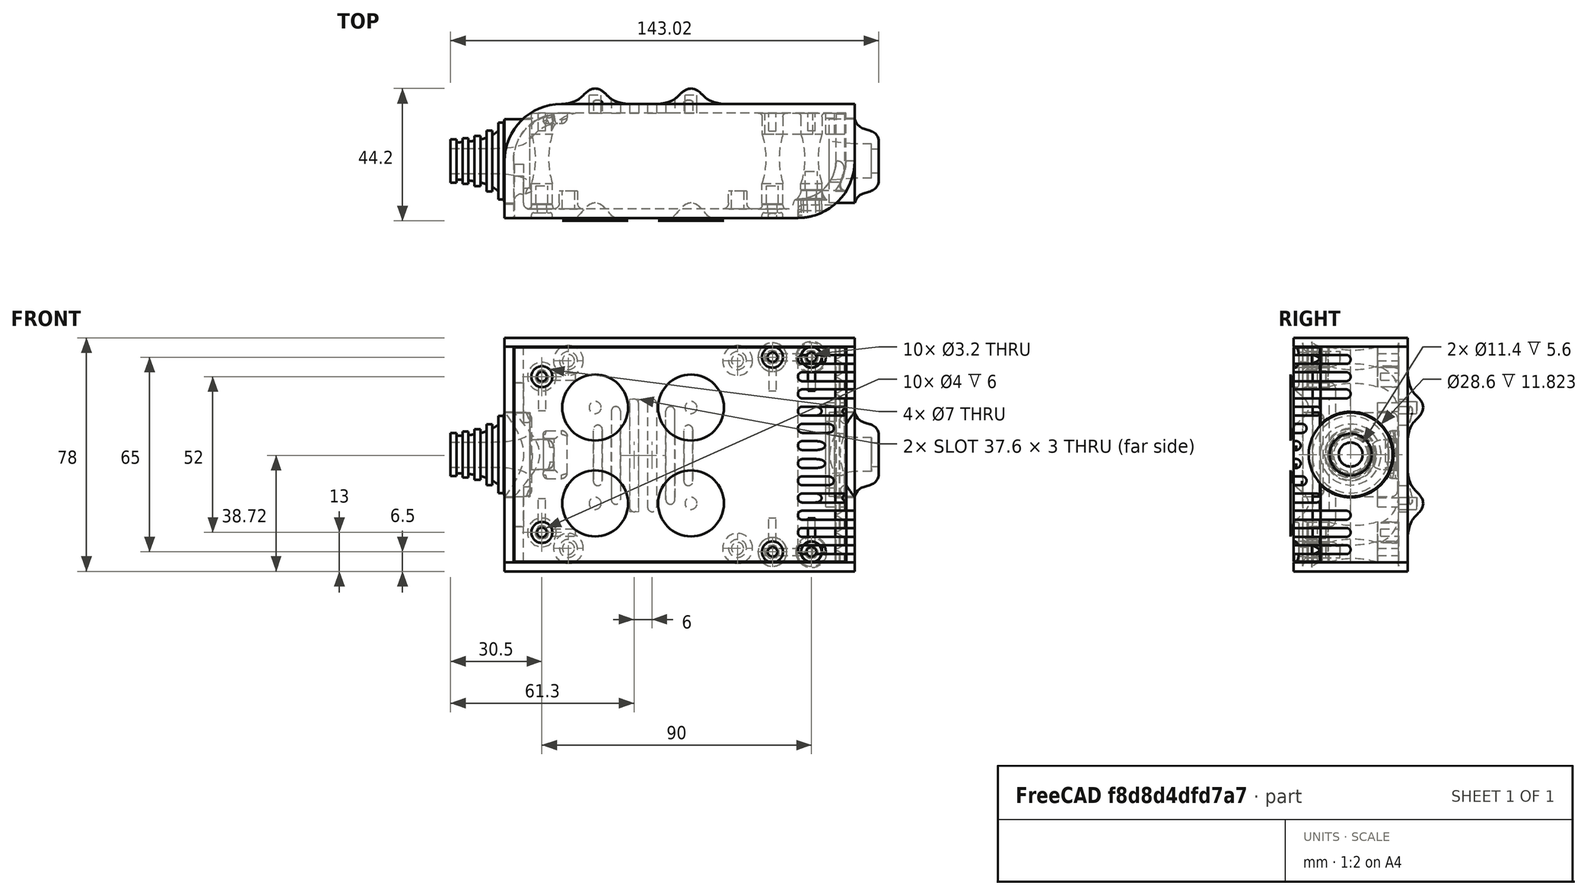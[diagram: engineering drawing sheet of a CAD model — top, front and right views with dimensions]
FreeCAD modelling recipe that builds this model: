
FCSTD DOCUMENT  (FreeCAD 0.19R0.19.2)
Label: enclosure_121
License: All rights reserved
LicenseURL: http://en.wikipedia.org/wiki/All_rights_reserved
objects: Part::Feature×72, Part::Revolution×72, Part::MultiFuse×54, Sketcher::SketchObject×34, Part::Fillet×26, Part::Cut×24, Part::Extrusion×23, Part::Cylinder×22, Part::Box×12, App::MeasureDistance×4
note: 339 computed .brp shape members not serialized (recipe doc carries the construction recipe); baked Part::Feature solids carry a one-line shape summary decoded from their .brp

FEATURE [Sketcher::SketchObject] Sketch  label="topSketch"
  FullyConstrained = true
  sketch-geometry (13):
    g0: LineSegment StartX=117 StartY=19 StartZ=0 EndX=117 EndY=38 EndZ=0
    g1: ArcOfCircle CenterX=98 CenterY=19 CenterZ=0 NormalX=0 NormalY=0 NormalZ=1 AngleXU=0 Radius=19 StartAngle=5.7297 EndAngle=6.28319
    g2: LineSegment StartX=0 StartY=3 StartZ=0 EndX=0 EndY=19 EndZ=0
    g3: LineSegment StartX=19 StartY=38 StartZ=0 EndX=117 EndY=38 EndZ=0
    g4: ArcOfCircle CenterX=19 CenterY=19 CenterZ=0 NormalX=0 NormalY=0 NormalZ=1 AngleXU=0 Radius=19 StartAngle=1.5708 EndAngle=3.14159
    g5: ArcOfCircle CenterX=19 CenterY=19 CenterZ=0 NormalX=0 NormalY=0 NormalZ=1 AngleXU=0 Radius=16 StartAngle=1.5708 EndAngle=3.14159
    g6: ArcOfCircle CenterX=98 CenterY=19 CenterZ=0 NormalX=0 NormalY=0 NormalZ=1 AngleXU=0 Radius=16 StartAngle=5.60905 EndAngle=6.28319
    g7: LineSegment StartX=114 StartY=19 StartZ=0 EndX=114 EndY=35 EndZ=0
    g8: LineSegment StartX=110.5 StartY=9.01251 StartZ=0 EndX=114.163 EndY=9.01251 EndZ=0
    g9: LineSegment StartX=114 StartY=35 StartZ=0 EndX=19 EndY=35 EndZ=0
    g10: LineSegment StartX=0 StartY=3 StartZ=0 EndX=0 EndY=0 EndZ=0
    g11: LineSegment StartX=3 StartY=0 StartZ=0 EndX=0 EndY=0 EndZ=0
    g12: LineSegment StartX=3 StartY=19 StartZ=0 EndX=3 EndY=0 EndZ=0
  constraints (33):
    c: Vertical(g0)
    c: Distance(g0) = 19
    c: Block(g0)
    c: Coincident(g1,g0)
    c: Block(g1)
    c: Vertical(g2)
    c: Block(g2)
    c: Coincident(g3,g0)
    c: Horizontal(g3)
    c: Distance(g3) = 98
    c: Coincident(g4,g3)
    c: Coincident(g4,g2)
    c: Block(g4)
    c: Coincident(g5,g4)
    c: Coincident(g6,g1)
    c: Block(g6)
    c: Block(g5)
    c: Coincident(g7,g6)
    c: Vertical(g7)
    c: Coincident(g8,g6)
    c: Coincident(g8,g1)
    c: Coincident(g9,g7)
    c: Coincident(g9,g5)
    c: Horizontal(g9)
    c: Tangent(g9,g5)
    c: Coincident(g10,g2)
    c: Distance(g10) = 3
    c: Vertical(g10)
    c: Coincident(g11,g10)
    c: Horizontal(g11)
    c: Coincident(g12,g5)
    c: Coincident(g12,g11)
    c: Vertical(g12)
FEATURE [Sketcher::SketchObject] Sketch001  label="bottomSketch"
  FullyConstrained = true
  sketch-geometry (32):
    g0: LineSegment StartX=3.3 StartY=-6.03275e-07 StartZ=0 EndX=98 EndY=-6.03275e-07 EndZ=0
    g1: ArcOfCircle CenterX=98 CenterY=19 CenterZ=0 NormalX=0 NormalY=0 NormalZ=1 AngleXU=0 Radius=19 StartAngle=4.71239 EndAngle=5.71103
    g2: LineSegment StartX=6.3 StartY=8 StartZ=0 EndX=3.3 EndY=8 EndZ=0
    g3: LineSegment StartX=3.3 StartY=8 StartZ=0 EndX=3.3 EndY=-6.03275e-07 EndZ=0
    g4: ArcOfCircle CenterX=8.3 CenterY=5 CenterZ=0 NormalX=0 NormalY=0 NormalZ=1 AngleXU=0 Radius=2 StartAngle=3.14159 EndAngle=4.71239
    g5: LineSegment StartX=6.3 StartY=8 StartZ=0 EndX=6.3 EndY=5 EndZ=0
    g6: ArcOfCircle CenterX=98 CenterY=19 CenterZ=0 NormalX=0 NormalY=0 NormalZ=1 AngleXU=0 Radius=12.7 StartAngle=4.71239 EndAngle=6.28319
    g7: LineSegment StartX=94.7 StartY=3 StartZ=0 EndX=8.3 EndY=3 EndZ=0
    g8-g12: Circle x5 (B-spline internal-alignment scaffolding for g13; pole/knot coordinates omitted)
    g13: BSplineCurve PolesCount=5 KnotsCount=3 Degree=3 IsPeriodic=0
    g14: GeomPoint X=98 Y=6.3 Z=0
    g15: GeomPoint X=96.3938 Y=4.71946 Z=0
    g16: GeomPoint X=94.7 Y=3 Z=0
    g17-g23: Circle x7 (B-spline internal-alignment scaffolding for g24; pole/knot coordinates omitted)
    g24: BSplineCurve PolesCount=7 KnotsCount=5 Degree=3 IsPeriodic=0
    g25-g29: GeomPoint x5 (B-spline internal-alignment scaffolding for g24; pole/knot coordinates omitted)
    g30: ArcOfCircle CenterX=98 CenterY=19 CenterZ=0 NormalX=0 NormalY=0 NormalZ=1 AngleXU=0 Radius=15.7 StartAngle=5.81226 EndAngle=6.28319
    g31: LineSegment StartX=110.7 StartY=19 StartZ=0 EndX=113.7 EndY=19 EndZ=0
  constraints (41):
    c: Horizontal(g0)
    c: Coincident(g1,g0)
    c: Block(g1)
    c: Horizontal(g2)
    c: Distance(g2) = 3
    c: Coincident(g3,g2)
    c: Vertical(g3)
    c: Coincident(g3,g0)
    c: Block(g4)
    c: Block(g2)
    c: Coincident(g5,g2)
    c: Coincident(g5,g4)
    c: Vertical(g5)
    c: Coincident(g6,g1)
    c: Block(g6)
    c: Coincident(g7,g4)
    c: Horizontal(g7)
    c: Block(g0)
    c: Block(g7)
    c: Block(g3)
    c: Coincident(g13,g6)
    c: Weight(g8) = 1
    c: Equal(g8, g9-g12) x4
    c: Coincident(g13,g7)
    c: InternalAlignment(g8-g12 -> g13) x5
    c: InternalAlignment(g14,g13)
    c: InternalAlignment(g15,g13)
    c: InternalAlignment(g16,g13)
    c: Block(g13)
    c: Weight(g17) = 1
    c: Equal(g17, g18-g23) x6
    c: Coincident(g24,g1)
    c: InternalAlignment(g17-g23 -> g24) x7
    c: InternalAlignment(g25-g29 -> g24) x5
    c: Block(g24)
    c: Coincident(g30,g24)
    c: Coincident(g31,g6)
    c: Coincident(g31,g30)
    c: Horizontal(g31)
    c: Block(g31)
    c: Block(g30)
FEATURE [Part::Extrusion] Extrude  label="top"
  Base = -> Sketch
  Dir = (0,0,1)
  DirMode = 2
  FaceMakerClass = Part::FaceMakerBullseye
  LengthFwd = 72
  LengthRev = 0
  Solid = true
  Symmetric = false
FEATURE [Part::Extrusion] Extrude001  label="bottom"
  Base = -> Sketch001
  Dir = (0,0,1)
  DirMode = 2
  FaceMakerClass = Part::FaceMakerBullseye
  LengthFwd = 71.4
  LengthRev = 0
  Placement = pos=(0,0,0.3) rot=(0,0,1;0rad)
  Solid = true
  Symmetric = false
FEATURE [Sketcher::SketchObject] Sketch002  label="topSketch001"
  FullyConstrained = true
  sketch-geometry (6):
    g0: LineSegment StartX=19 StartY=38 StartZ=0 EndX=117 EndY=38 EndZ=0
    g1: ArcOfCircle CenterX=19 CenterY=19 CenterZ=0 NormalX=0 NormalY=0 NormalZ=1 AngleXU=0 Radius=19 StartAngle=1.5708 EndAngle=3.14159
    g2: LineSegment StartX=117 StartY=38 StartZ=0 EndX=117 EndY=19 EndZ=0
    g3: LineSegment StartX=98 StartY=1.0161e-12 StartZ=0 EndX=5.22862e-06 EndY=1.0161e-12 EndZ=0
    g4: LineSegment StartX=5.22862e-06 StartY=19 StartZ=0 EndX=5.22862e-06 EndY=1.0161e-12 EndZ=0
    g5: ArcOfCircle CenterX=98 CenterY=19 CenterZ=0 NormalX=0 NormalY=0 NormalZ=1 AngleXU=0 Radius=19 StartAngle=4.71239 EndAngle=6.28319
  constraints (16):
    c: Horizontal(g0)
    c: Distance(g0) = 98
    c: Coincident(g1,g0)
    c: Block(g1)
    c: Coincident(g2,g0)
    c: Vertical(g2)
    c: Distance(g2) = 19
    c: Horizontal(g3)
    c: Coincident(g4,g1)
    c: Vertical(g4)
    c: Coincident(g3,g4)
    c: Block(g3)
    c: Coincident(g5,g2)
    c: Coincident(g5,g3)
    c: Block(g0)
    c: Block(g5)
FEATURE [Part::Extrusion] Extrude002  label="sideA"
  Base = -> Sketch002
  Dir = (0,0,1)
  DirMode = 2
  FaceMakerClass = Part::FaceMakerBullseye
  LengthFwd = 3
  LengthRev = 0
  Placement = pos=(0,0,-3) rot=(0,0,1;0rad)
  Solid = true
  Symmetric = false
FEATURE [Sketcher::SketchObject] Sketch003  label="topSketch002"
  FullyConstrained = true
  sketch-geometry (6):
    g0: LineSegment StartX=19 StartY=38 StartZ=0 EndX=117 EndY=38 EndZ=0
    g1: ArcOfCircle CenterX=19 CenterY=19 CenterZ=0 NormalX=0 NormalY=0 NormalZ=1 AngleXU=0 Radius=19 StartAngle=1.5708 EndAngle=3.14159
    g2: LineSegment StartX=117 StartY=38 StartZ=0 EndX=117 EndY=19 EndZ=0
    g3: LineSegment StartX=98 StartY=1.0161e-12 StartZ=0 EndX=5.22862e-06 EndY=1.0161e-12 EndZ=0
    g4: LineSegment StartX=5.22862e-06 StartY=19 StartZ=0 EndX=5.22862e-06 EndY=1.0161e-12 EndZ=0
    g5: ArcOfCircle CenterX=98 CenterY=19 CenterZ=0 NormalX=0 NormalY=0 NormalZ=1 AngleXU=0 Radius=19 StartAngle=4.71239 EndAngle=6.28319
  constraints (16):
    c: Horizontal(g0)
    c: Distance(g0) = 98
    c: Coincident(g1,g0)
    c: Block(g1)
    c: Coincident(g2,g0)
    c: Vertical(g2)
    c: Distance(g2) = 19
    c: Horizontal(g3)
    c: Coincident(g4,g1)
    c: Vertical(g4)
    c: Coincident(g3,g4)
    c: Block(g3)
    c: Coincident(g5,g2)
    c: Coincident(g5,g3)
    c: Block(g0)
    c: Block(g5)
FEATURE [Part::Extrusion] Extrude003  label="sideB"
  Base = -> Sketch003
  Dir = (0,0,1)
  DirMode = 2
  FaceMakerClass = Part::FaceMakerBullseye
  LengthFwd = 3
  LengthRev = 0
  Placement = pos=(0,0,72) rot=(0,0,1;0rad)
  Solid = true
  Symmetric = false
FEATURE [Sketcher::SketchObject] Sketch004
  FullyConstrained = true
  MapMode = 3
  Placement = pos=(0,0,0) rot=(1,0,0;1.5708rad)
  Support = -> [Extrude]
  sketch-geometry (8):
    g0: Circle CenterX=80.351 CenterY=-67.6202 CenterZ=0 NormalX=0 NormalY=0 NormalZ=1 AngleXU=0 Radius=2
    g1: Circle CenterX=80.351 CenterY=-67.6202 CenterZ=0 NormalX=0 NormalY=0 NormalZ=1 AngleXU=0 Radius=3
    g2: Circle CenterX=80.351 CenterY=-4.92017 CenterZ=0 NormalX=0 NormalY=0 NormalZ=1 AngleXU=0 Radius=2
    g3: Circle CenterX=80.351 CenterY=-4.92017 CenterZ=0 NormalX=0 NormalY=0 NormalZ=1 AngleXU=0 Radius=3
    g4: Circle CenterX=23.851 CenterY=-4.92017 CenterZ=0 NormalX=0 NormalY=0 NormalZ=1 AngleXU=0 Radius=2
    g5: Circle CenterX=23.851 CenterY=-4.92017 CenterZ=0 NormalX=0 NormalY=0 NormalZ=1 AngleXU=0 Radius=3
    g6: Circle CenterX=23.851 CenterY=-67.6202 CenterZ=0 NormalX=0 NormalY=0 NormalZ=1 AngleXU=0 Radius=2
    g7: Circle CenterX=23.851 CenterY=-67.6202 CenterZ=0 NormalX=0 NormalY=0 NormalZ=1 AngleXU=0 Radius=3
  constraints (8):
    c: Block(g3)
    c: Block(g2)
    c: Block(g1)
    c: Block(g0)
    c: Block(g6)
    c: Block(g7)
    c: Block(g4)
    c: Block(g5)
FEATURE [Part::Extrusion] Extrude004
  Base = -> Sketch004
  Dir = (0,-1,2e-16)
  DirMode = 2
  FaceMakerClass = Part::FaceMakerBullseye
  LengthFwd = 6
  LengthRev = 0
  Placement = pos=(0,9,0) rot=(0,0,1;0rad)
  Solid = true
  Symmetric = false
FEATURE [Sketcher::SketchObject] Sketch005
  FullyConstrained = true
  MapMode = 3
  Placement = pos=(0,0,0) rot=(1,0,0;1.5708rad)
  Support = -> [Extrude]
  sketch-geometry (8):
    g0: Circle CenterX=80.351 CenterY=-67.6202 CenterZ=0 NormalX=0 NormalY=0 NormalZ=1 AngleXU=0 Radius=3
    g1: Circle CenterX=80.351 CenterY=-4.92017 CenterZ=0 NormalX=0 NormalY=0 NormalZ=1 AngleXU=0 Radius=3
    g2: Circle CenterX=23.851 CenterY=-4.92017 CenterZ=0 NormalX=0 NormalY=0 NormalZ=1 AngleXU=0 Radius=3
    g3: Circle CenterX=23.851 CenterY=-67.6202 CenterZ=0 NormalX=0 NormalY=0 NormalZ=1 AngleXU=0 Radius=3
    g4: Circle CenterX=23.851 CenterY=-67.6202 CenterZ=0 NormalX=0 NormalY=0 NormalZ=1 AngleXU=0 Radius=5
    g5: Circle CenterX=80.351 CenterY=-67.6202 CenterZ=0 NormalX=0 NormalY=0 NormalZ=1 AngleXU=0 Radius=5
    g6: Circle CenterX=23.851 CenterY=-4.92017 CenterZ=0 NormalX=0 NormalY=0 NormalZ=1 AngleXU=0 Radius=5
    g7: Circle CenterX=80.351 CenterY=-4.92017 CenterZ=0 NormalX=0 NormalY=0 NormalZ=1 AngleXU=0 Radius=5
  constraints (8):
    c: Block(g1)
    c: Block(g0)
    c: Block(g3)
    c: Block(g2)
    c: Block(g5)
    c: Block(g4)
    c: Block(g6)
    c: Block(g7)
FEATURE [Part::Extrusion] Extrude005
  Base = -> Sketch005
  Dir = (0,-1,2e-16)
  DirMode = 2
  FaceMakerClass = Part::FaceMakerBullseye
  LengthFwd = 2
  LengthRev = 0
  Solid = true
  Symmetric = false
FEATURE [Sketcher::SketchObject] Sketch006
  FullyConstrained = true
  MapMode = 3
  Placement = pos=(0,0,0) rot=(1,0,0;1.5708rad)
  sketch-geometry (8):
    g0: Circle CenterX=80.351 CenterY=-67.6202 CenterZ=0 NormalX=0 NormalY=0 NormalZ=1 AngleXU=0 Radius=3
    g1: Circle CenterX=80.351 CenterY=-4.92017 CenterZ=0 NormalX=0 NormalY=0 NormalZ=1 AngleXU=0 Radius=3
    g2: Circle CenterX=23.851 CenterY=-4.92017 CenterZ=0 NormalX=0 NormalY=0 NormalZ=1 AngleXU=0 Radius=3
    g3: Circle CenterX=23.851 CenterY=-67.6202 CenterZ=0 NormalX=0 NormalY=0 NormalZ=1 AngleXU=0 Radius=3
    g4: Circle CenterX=23.851 CenterY=-67.6202 CenterZ=0 NormalX=0 NormalY=0 NormalZ=1 AngleXU=0 Radius=5
    g5: Circle CenterX=80.351 CenterY=-67.6202 CenterZ=0 NormalX=0 NormalY=0 NormalZ=1 AngleXU=0 Radius=5
    g6: Circle CenterX=23.851 CenterY=-4.92017 CenterZ=0 NormalX=0 NormalY=0 NormalZ=1 AngleXU=0 Radius=5
    g7: Circle CenterX=80.351 CenterY=-4.92017 CenterZ=0 NormalX=0 NormalY=0 NormalZ=1 AngleXU=0 Radius=5
  constraints (8):
    c: Block(g1)
    c: Block(g0)
    c: Block(g3)
    c: Block(g2)
    c: Block(g5)
    c: Block(g4)
    c: Block(g6)
    c: Block(g7)
FEATURE [Part::Extrusion] Extrude007
  Base = -> Sketch006
  Dir = (0,-1,2e-16)
  DirMode = 2
  FaceMakerClass = Part::FaceMakerBullseye
  LengthFwd = 2
  LengthRev = 0
  Solid = true
  Symmetric = false
FEATURE [Part::Fillet] Fillet
  Base = -> Extrude007
  Edges = 4 edges r=1.99: [Edge6,Edge12,Edge18,Edge24]
FEATURE [Part::Cut] Cut
  Base = -> Extrude005
  Placement = pos=(0,5,0) rot=(0,0,1;0rad)
  Tool = -> Fillet
FEATURE [Part::MultiFuse] Fusion  label="pCBScrews"
  Placement = pos=(-2.5,0,72.3) rot=(0,0,1;0rad)
  Shapes = -> [Extrude004,Cut]
FEATURE [App::MeasureDistance] Distance  label="Distance: 0.69 mm"
  Distance = 0.685967
  P1 = (24.0138,2.9647,0.3)
  P2 = (23.8901,3,-0.373787)
FEATURE [App::MeasureDistance] Distance001  label="Distance: 0.53 mm"
  Distance = 0.533607
  P1 = (80.2939,3,72.2334)
  P2 = (80.281,2.99661,71.7)
FEATURE [Part::Fillet] Fillet001
  Base = -> Extrude001
  Edges = 1 edges r=2.4: [Edge17]
FEATURE [Part::Fillet] Fillet002  label="bottom001"
  Base = -> Fillet001
  Edges = 1 edges r=2.4: [Edge36]
FEATURE [Part::Fillet] Fillet003  label="top001"
  Base = -> Extrude
  Edges = 1 edges r=2: [Edge1]
FEATURE [Sketcher::SketchObject] Sketch007
  FullyConstrained = true
  sketch-geometry (16):
    g0: LineSegment StartX=4 StartY=0 StartZ=0 EndX=4 EndY=2.4 EndZ=0
    g1: LineSegment StartX=4 StartY=2.4 StartZ=0 EndX=7 EndY=2.4 EndZ=0
    g2: LineSegment StartX=4 StartY=0 StartZ=0 EndX=5.7 EndY=0 EndZ=0
    g3: LineSegment StartX=5.7 StartY=0 StartZ=0 EndX=5.7 EndY=-5.6 EndZ=0
    g4-g8: Circle x5 (B-spline internal-alignment scaffolding for g9; pole/knot coordinates omitted)
    g9: BSplineCurve PolesCount=5 KnotsCount=3 Degree=3 IsPeriodic=0
    g10: GeomPoint X=7 Y=2.4 Z=0
    g11: GeomPoint X=10.4582 Y=-1.55472 Z=0
    g12: GeomPoint X=14 Y=-5.6 Z=0
    g13: LineSegment StartX=14 StartY=-5.6 StartZ=0 EndX=14 EndY=-14.1 EndZ=0
    g14: LineSegment StartX=14 StartY=-14.1 StartZ=0 EndX=6.5 EndY=-14.1 EndZ=0
    g15: LineSegment StartX=5.7 StartY=-5.6 StartZ=0 EndX=6.5 EndY=-14.1 EndZ=0
  constraints (28):
    c: Distance(g0) = 2.4
    c: Vertical(g0)
    c: Block(g0)
    c: Coincident(g1,g0)
    c: Horizontal(g1)
    c: Distance(g1) = 3
    c: Coincident(g2,g0)
    c: Horizontal(g2)
    c: Distance(g2) = 1.7
    c: Coincident(g3,g2)
    c: Vertical(g3)
    c: Distance(g3) = 5.6
    c: Coincident(g9,g1)
    c: Weight(g4) = 1
    c: Equal(g4, g5-g8) x4
    c: InternalAlignment(g4-g8 -> g9) x5
    c: InternalAlignment(g10,g9)
    c: InternalAlignment(g11,g9)
    c: InternalAlignment(g12,g9)
    c: Block(g9)
    c: Coincident(g13,g9)
    c: Vertical(g13)
    c: Distance(g13) = 8.5
    c: Coincident(g14,g13)
    c: Horizontal(g14)
    c: Distance(g14) = 7.5
    c: Coincident(g15,g3)
    c: Coincident(g15,g14)
FEATURE [Part::Feature] Face
  shape: bbox 10 x 16.5 x 2e-07 mm, 1 faces, 0 solids (baked)
FEATURE [Part::Revolution] Revolve  label="plugHousing"
  Angle = 360
  Axis = (0,1,0)
  Base = (0,0,0)
  FaceMakerClass = Part::FaceMakerBullseye
  Placement = pos=(0,0,36.15) rot=(0,0,1;0rad)
  Solid = false
  Source = -> Face
  Symmetric = false
FEATURE [Part::Feature] Face001
  shape: bbox 10 x 16.5 x 2e-07 mm, 1 faces, 0 solids (baked)
FEATURE [Part::Revolution] Revolve001  label="plugHousing001"
  Angle = 360
  Axis = (0,1,0)
  Base = (0,0,0)
  FaceMakerClass = Part::FaceMakerBullseye
  Placement = pos=(0,0,36.15) rot=(0,0,1;0rad)
  Solid = false
  Source = -> Face001
  Symmetric = false
FEATURE [Part::MultiFuse] Fusion001  label="plugHousing002"
  Placement = pos=(0,0,0) rot=(0,0,1;1.5708rad)
  Shapes = -> [Revolve001,Revolve]
FEATURE [Part::Feature] Face002
  shape: bbox 10 x 16.5 x 2e-07 mm, 1 faces, 0 solids (baked)
FEATURE [Part::Revolution] Revolve003  label="plugHousing005"
  Angle = 360
  Axis = (0,1,0)
  Base = (0,0,0)
  FaceMakerClass = Part::FaceMakerBullseye
  Placement = pos=(0,0,36.15) rot=(0,0,1;0rad)
  Solid = false
  Source = -> Face002
  Symmetric = false
FEATURE [Part::Feature] Face003
  shape: bbox 10 x 16.5 x 2e-07 mm, 1 faces, 0 solids (baked)
FEATURE [Part::Revolution] Revolve002  label="plugHousing003"
  Angle = 360
  Axis = (0,1,0)
  Base = (0,0,0)
  FaceMakerClass = Part::FaceMakerBullseye
  Placement = pos=(0,0,36.15) rot=(0,0,1;0rad)
  Solid = false
  Source = -> Face003
  Symmetric = false
FEATURE [Part::MultiFuse] Fusion002  label="plugHousing004"
  Placement = pos=(0,0,0) rot=(0,0,1;1.5708rad)
  Shapes = -> [Revolve002,Revolve003]
FEATURE [Part::MultiFuse] Fusion003  label="plugHousing006"
  Placement = pos=(0,19,0) rot=(0,0,1;3.14159rad)
  Shapes = -> [Fusion002,Fusion001]
FEATURE [Part::Feature] Face004
  shape: bbox 10 x 16.5 x 2e-07 mm, 1 faces, 0 solids (baked)
FEATURE [Part::Revolution] Revolve006  label="plugHousing010"
  Angle = 360
  Axis = (0,1,0)
  Base = (0,0,0)
  FaceMakerClass = Part::FaceMakerBullseye
  Placement = pos=(0,0,36.15) rot=(0,0,1;0rad)
  Solid = false
  Source = -> Face004
  Symmetric = false
FEATURE [Part::Feature] Face005
  shape: bbox 10 x 16.5 x 2e-07 mm, 1 faces, 0 solids (baked)
FEATURE [Part::Revolution] Revolve007  label="plugHousing011"
  Angle = 360
  Axis = (0,1,0)
  Base = (0,0,0)
  FaceMakerClass = Part::FaceMakerBullseye
  Placement = pos=(0,0,36.15) rot=(0,0,1;0rad)
  Solid = false
  Source = -> Face005
  Symmetric = false
FEATURE [Part::Feature] Face006
  shape: bbox 10 x 16.5 x 2e-07 mm, 1 faces, 0 solids (baked)
FEATURE [Part::Revolution] Revolve004  label="plugHousing007"
  Angle = 360
  Axis = (0,1,0)
  Base = (0,0,0)
  FaceMakerClass = Part::FaceMakerBullseye
  Placement = pos=(0,0,36.15) rot=(0,0,1;0rad)
  Solid = false
  Source = -> Face006
  Symmetric = false
FEATURE [Part::MultiFuse] Fusion004  label="plugHousing009"
  Placement = pos=(0,0,0) rot=(0,0,1;1.5708rad)
  Shapes = -> [Revolve004,Revolve007]
FEATURE [Part::Feature] Face007
  shape: bbox 10 x 16.5 x 2e-07 mm, 1 faces, 0 solids (baked)
FEATURE [Part::Revolution] Revolve005  label="plugHousing008"
  Angle = 360
  Axis = (0,1,0)
  Base = (0,0,0)
  FaceMakerClass = Part::FaceMakerBullseye
  Placement = pos=(0,0,36.15) rot=(0,0,1;0rad)
  Solid = false
  Source = -> Face007
  Symmetric = false
FEATURE [Part::MultiFuse] Fusion005  label="plugHousing012"
  Placement = pos=(0,0,0) rot=(0,0,1;1.5708rad)
  Shapes = -> [Revolve006,Revolve005]
FEATURE [Part::MultiFuse] Fusion006  label="plugHousing013"
  Placement = pos=(0,19,0) rot=(0,0,1;3.14159rad)
  Shapes = -> [Fusion005,Fusion004]
FEATURE [Part::MultiFuse] Fusion007  label="plugHousing014"
  Placement = pos=(122.621,0,-0.15) rot=(0,0,1;0rad)
  Shapes = -> [Fusion003,Fusion006]
FEATURE [Part::Cylinder] Cylinder002
  Angle = 360
  AttacherType = Attacher::AttachEngine3D
  Height = 20
  Placement = pos=(0,0,36.15) rot=(0,0,1;0rad)
  Radius = 4
FEATURE [Part::Cylinder] Cylinder003
  Angle = 360
  AttacherType = Attacher::AttachEngine3D
  Height = 10
  Placement = pos=(0,0,36.15) rot=(0,0,1;0rad)
  Radius = 4
FEATURE [Part::MultiFuse] Fusion009  label="removeToCreateHoleForPlugHousing"
  Placement = pos=(70,19,36.15) rot=(0,1,0;1.5708rad)
  Shapes = -> [Cylinder002,Cylinder003]
FEATURE [Part::Cylinder] Cylinder004
  Angle = 360
  AttacherType = Attacher::AttachEngine3D
  Height = 20
  Placement = pos=(0,0,36.15) rot=(0,0,1;0rad)
  Radius = 4
FEATURE [Part::Cylinder] Cylinder005
  Angle = 360
  AttacherType = Attacher::AttachEngine3D
  Height = 10
  Placement = pos=(0,0,36.15) rot=(0,0,1;0rad)
  Radius = 4
FEATURE [Part::MultiFuse] Fusion010  label="removeToCreateHoleForPlugHousing001"
  Placement = pos=(70,19,36.15) rot=(0,1,0;1.5708rad)
  Shapes = -> [Cylinder004,Cylinder005]
FEATURE [Part::Cut] Cut001
  Base = -> Fillet003
  Tool = -> Fusion010
FEATURE [Part::Cut] Cut002  label="Bottom"
  Base = -> Fillet002
  Tool = -> Fusion009
FEATURE [Part::Feature] Face008
  shape: bbox 10 x 16.5 x 2e-07 mm, 1 faces, 0 solids (baked)
FEATURE [Part::Revolution] Revolve011  label="plugHousing021"
  Angle = 360
  Axis = (0,1,0)
  Base = (0,0,0)
  FaceMakerClass = Part::FaceMakerBullseye
  Placement = pos=(0,0,36.15) rot=(0,0,1;0rad)
  Solid = false
  Source = -> Face008
  Symmetric = false
FEATURE [Part::Feature] Face009
  shape: bbox 10 x 16.5 x 2e-07 mm, 1 faces, 0 solids (baked)
FEATURE [Part::Revolution] Revolve012  label="plugHousing022"
  Angle = 360
  Axis = (0,1,0)
  Base = (0,0,0)
  FaceMakerClass = Part::FaceMakerBullseye
  Placement = pos=(0,0,36.15) rot=(0,0,1;0rad)
  Solid = false
  Source = -> Face009
  Symmetric = false
FEATURE [Part::Feature] Face010 .. Face013  x4 (patterned run collapsed; names and placements below)
  shape: bbox 10 x 16.5 x 2e-07 mm, 1 faces, 0 solids (baked)
FEATURE [Part::Revolution] Revolve015  label="plugHousing027"
  Angle = 360
  Axis = (0,1,0)
  Base = (0,0,0)
  FaceMakerClass = Part::FaceMakerBullseye
  Placement = pos=(0,0,36.15) rot=(0,0,1;0rad)
  Solid = false
  Source = -> Face013
  Symmetric = false
FEATURE [Part::Feature] Face014
  shape: bbox 10 x 16.5 x 2e-07 mm, 1 faces, 0 solids (baked)
FEATURE [Part::Feature] Face015
  shape: bbox 10 x 16.5 x 2e-07 mm, 1 faces, 0 solids (baked)
FEATURE [Part::Feature] Face016
  shape: bbox 10 x 16.5 x 2e-07 mm, 1 faces, 0 solids (baked)
FEATURE [Part::Revolution] Revolve019  label="plugHousing033"
  Angle = 360
  Axis = (0,1,0)
  Base = (0,0,0)
  FaceMakerClass = Part::FaceMakerBullseye
  Placement = pos=(0,0,36.15) rot=(0,0,1;0rad)
  Solid = false
  Source = -> Face016
  Symmetric = false
FEATURE [Part::Feature] Face017
  shape: bbox 10 x 16.5 x 2e-07 mm, 1 faces, 0 solids (baked)
FEATURE [Part::Revolution] Revolve020  label="plugHousing034"
  Angle = 360
  Axis = (0,1,0)
  Base = (0,0,0)
  FaceMakerClass = Part::FaceMakerBullseye
  Placement = pos=(0,0,36.15) rot=(0,0,1;0rad)
  Solid = false
  Source = -> Face017
  Symmetric = false
FEATURE [Part::Feature] Face018
  shape: bbox 10 x 16.5 x 2e-07 mm, 1 faces, 0 solids (baked)
FEATURE [Part::Revolution] Revolve016  label="plugHousing030"
  Angle = 360
  Axis = (0,1,0)
  Base = (0,0,0)
  FaceMakerClass = Part::FaceMakerBullseye
  Placement = pos=(0,0,36.15) rot=(0,0,1;0rad)
  Solid = false
  Source = -> Face018
  Symmetric = false
FEATURE [Part::MultiFuse] Fusion020  label="plugHousing038"
  Placement = pos=(0,0,0) rot=(0,0,1;1.5708rad)
  Shapes = -> [Revolve016,Revolve020]
FEATURE [Part::Feature] Face019
  shape: bbox 10 x 16.5 x 2e-07 mm, 1 faces, 0 solids (baked)
FEATURE [Part::Feature] Face020
  shape: bbox 10 x 16.5 x 2e-07 mm, 1 faces, 0 solids (baked)
FEATURE [Part::Revolution] Revolve017  label="plugHousing031"
  Angle = 360
  Axis = (0,1,0)
  Base = (0,0,0)
  FaceMakerClass = Part::FaceMakerBullseye
  Placement = pos=(0,0,36.15) rot=(0,0,1;0rad)
  Solid = false
  Source = -> Face020
  Symmetric = false
FEATURE [Part::MultiFuse] Fusion021  label="plugHousing039"
  Placement = pos=(0,0,0) rot=(0,0,1;1.5708rad)
  Shapes = -> [Revolve019,Revolve017]
FEATURE [Part::MultiFuse] Fusion023  label="plugHousing041"
  Placement = pos=(0,19,0) rot=(0,0,1;3.14159rad)
  Shapes = -> [Fusion021,Fusion020]
FEATURE [Part::Revolution] Revolve022  label="plugHousing043"
  Angle = 360
  Axis = (0,1,0)
  Base = (0,0,0)
  FaceMakerClass = Part::FaceMakerBullseye
  Placement = pos=(0,0,36.15) rot=(0,0,1;0rad)
  Solid = false
  Source = -> Face019
  Symmetric = false
FEATURE [Part::Feature] Face021
  shape: bbox 10 x 16.5 x 2e-07 mm, 1 faces, 0 solids (baked)
FEATURE [Part::Revolution] Revolve023  label="plugHousing044"
  Angle = 360
  Axis = (0,1,0)
  Base = (0,0,0)
  FaceMakerClass = Part::FaceMakerBullseye
  Placement = pos=(0,0,36.15) rot=(0,0,1;0rad)
  Solid = false
  Source = -> Face021
  Symmetric = false
FEATURE [Part::Feature] Face022
  shape: bbox 10 x 16.5 x 2e-07 mm, 1 faces, 0 solids (baked)
FEATURE [Part::Revolution] Revolve018  label="plugHousing032"
  Angle = 360
  Axis = (0,1,0)
  Base = (0,0,0)
  FaceMakerClass = Part::FaceMakerBullseye
  Placement = pos=(0,0,36.15) rot=(0,0,1;0rad)
  Solid = false
  Source = -> Face022
  Symmetric = false
FEATURE [Part::MultiFuse] Fusion022  label="plugHousing040"
  Placement = pos=(0,0,0) rot=(0,0,1;1.5708rad)
  Shapes = -> [Revolve018,Revolve023]
FEATURE [Part::Feature] Face023
  shape: bbox 10 x 16.5 x 2e-07 mm, 1 faces, 0 solids (baked)
FEATURE [Part::Revolution] Revolve021  label="plugHousing035"
  Angle = 360
  Axis = (0,1,0)
  Base = (0,0,0)
  FaceMakerClass = Part::FaceMakerBullseye
  Placement = pos=(0,0,36.15) rot=(0,0,1;0rad)
  Solid = false
  Source = -> Face023
  Symmetric = false
FEATURE [Part::MultiFuse] Fusion018  label="plugHousing036"
  Placement = pos=(0,0,0) rot=(0,0,1;1.5708rad)
  Shapes = -> [Revolve022,Revolve021]
FEATURE [Part::MultiFuse] Fusion019  label="plugHousing037"
  Placement = pos=(0,19,0) rot=(0,0,1;3.14159rad)
  Shapes = -> [Fusion018,Fusion022]
FEATURE [Part::MultiFuse] Fusion024  label="plugHousing042"
  Placement = pos=(122.621,0,-0.15) rot=(0,0,1;0rad)
  Shapes = -> [Fusion023,Fusion019]
FEATURE [Part::Cylinder] Cylinder006
  Angle = 360
  AttacherType = Attacher::AttachEngine3D
  Height = 20
  Placement = pos=(0,0,36.15) rot=(0,0,1;0rad)
  Radius = 14.3
FEATURE [Part::Cylinder] Cylinder007
  Angle = 360
  AttacherType = Attacher::AttachEngine3D
  Height = 10
  Placement = pos=(0,0,36.15) rot=(0,0,1;0rad)
  Radius = 4
FEATURE [Part::MultiFuse] Fusion026  label="removeToCreteHoleForPlugHousing"
  Placement = pos=(70,19,36) rot=(0,1,0;1.5708rad)
  Shapes = -> [Cylinder006,Cylinder007]
FEATURE [Part::Box] Box001  label="Cube001"
  AttacherType = Attacher::AttachEngine3D
  Height = 28
  Length = 3
  Placement = pos=(110.7,19,22) rot=(0,0,1;0rad)
  Width = 15.7
FEATURE [Part::Cut] Cut003  label="top002"
  Base = -> Cut001
  Tool = -> Fusion007
FEATURE [Part::Revolution] Revolve008  label="plugHousing015"
  Angle = 360
  Axis = (0,1,0)
  Base = (0,0,0)
  FaceMakerClass = Part::FaceMakerBullseye
  Placement = pos=(0,0,36.15) rot=(0,0,1;0rad)
  Solid = false
  Source = -> Face010
  Symmetric = false
FEATURE [Part::MultiFuse] Fusion013  label="plugHousing020"
  Placement = pos=(0,0,0) rot=(0,0,1;1.5708rad)
  Shapes = -> [Revolve008,Revolve012]
FEATURE [Part::Cut] Cut004  label="top003"
  Base = -> Cut003
  Placement = pos=(1,0,0) rot=(0,0,1;0rad)
  Tool = -> Fusion026
FEATURE [Part::Cylinder] Cylinder008
  Angle = 360
  AttacherType = Attacher::AttachEngine3D
  Height = 20
  Placement = pos=(0,0,36.15) rot=(0,0,1;0rad)
  Radius = 10.3
FEATURE [Part::Cylinder] Cylinder009
  Angle = 360
  AttacherType = Attacher::AttachEngine3D
  Height = 10
  Placement = pos=(0,0,36.15) rot=(0,0,1;0rad)
  Radius = 4
FEATURE [Part::MultiFuse] Fusion027  label="removeToCreteHoleForPlugHousing001"
  Placement = pos=(70,19,36) rot=(0,1,0;1.5708rad)
  Shapes = -> [Cylinder008,Cylinder009]
FEATURE [Part::Cut] Cut005  label="plugHousingTab"
  Base = -> Box001
  Tool = -> Fusion027
FEATURE [Part::MultiFuse] Fusion028  label="plugHousing045"
  Shapes = -> [Fusion024,Cut005]
FEATURE [Part::Box] Box002  label="Cube002"
  AttacherType = Attacher::AttachEngine3D
  Height = 28.8
  Length = 3
  Placement = pos=(107.3,28,21.6) rot=(0,0,1;0rad)
  Width = 7
FEATURE [Part::Box] Box003  label="Cube003"
  AttacherType = Attacher::AttachEngine3D
  Height = 3
  Length = 6.4
  Placement = pos=(107.3,28,18.6) rot=(0,0,1;0rad)
  Width = 7
FEATURE [Part::Box] Box004  label="Cube004"
  AttacherType = Attacher::AttachEngine3D
  Height = 3
  Length = 6.4
  Placement = pos=(107.3,28,50.4) rot=(0,0,1;0rad)
  Width = 7
FEATURE [Part::MultiFuse] Fusion029  label="plugHousingBracketHolder"
  Shapes = -> [Box004,Box002,Box003]
FEATURE [Part::Cylinder] Cylinder010
  Angle = 360
  AttacherType = Attacher::AttachEngine3D
  Height = 20
  Placement = pos=(0,0,36.15) rot=(0,0,1;0rad)
  Radius = 14.3
FEATURE [Part::Cylinder] Cylinder011
  Angle = 360
  AttacherType = Attacher::AttachEngine3D
  Height = 10
  Placement = pos=(0,0,36.15) rot=(0,0,1;0rad)
  Radius = 4
FEATURE [Part::MultiFuse] Fusion030  label="removeToCreteHoleForPlugHousing002"
  Placement = pos=(70,19,36) rot=(0,1,0;1.5708rad)
  Shapes = -> [Cylinder010,Cylinder011]
FEATURE [Part::Cut] Cut006  label="plugHousingBracketHolder001"
  Base = -> Fusion029
  Tool = -> Fusion030
FEATURE [Part::Cylinder] Cylinder012
  Angle = 360
  AttacherType = Attacher::AttachEngine3D
  Height = 20
  Placement = pos=(0,0,36.15) rot=(0,0,1;0rad)
  Radius = 7
FEATURE [Part::Cylinder] Cylinder013
  Angle = 360
  AttacherType = Attacher::AttachEngine3D
  Height = 10
  Placement = pos=(0,0,36.15) rot=(0,0,1;0rad)
  Radius = 4
FEATURE [Part::MultiFuse] Fusion032  label="removeToCreteHoleForPlugHousing003"
  Placement = pos=(70,19,36) rot=(0,1,0;1.5708rad)
  Shapes = -> [Cylinder012,Cylinder013]
FEATURE [Part::Cut] Cut007  label="bottom002"
  Base = -> Cut002
  Tool = -> Fusion032
FEATURE [Sketcher::SketchObject] Sketch008
  FullyConstrained = true
  sketch-geometry (54):
    g0: LineSegment StartX=-4.2 StartY=0 StartZ=0 EndX=-6.2 EndY=0 EndZ=0
    g1: LineSegment StartX=-14 StartY=-18 StartZ=0 EndX=-14 EndY=-26.5 EndZ=0
    g2: LineSegment StartX=-4.2 StartY=0 StartZ=0 EndX=-4.2 EndY=-13.4877 EndZ=0
    g3: Circle CenterX=-4.2 CenterY=-13.4877 CenterZ=0 NormalX=0 NormalY=0 NormalZ=1 AngleXU=0 Radius=1
    g4: Circle CenterX=-4.2 CenterY=-26.5 CenterZ=0 NormalX=0 NormalY=0 NormalZ=1 AngleXU=0 Radius=1
    g5: Circle CenterX=-8.2 CenterY=-26.5 CenterZ=0 NormalX=0 NormalY=0 NormalZ=1 AngleXU=0 Radius=1
    g6: BSplineCurve PolesCount=3 KnotsCount=2 Degree=2 IsPeriodic=0
    g7: GeomPoint X=-4.2 Y=-13.4877 Z=0
    g8: GeomPoint X=-8.2 Y=-26.5 Z=0
    g9: LineSegment StartX=-14 StartY=-26.5 StartZ=0 EndX=-8.2 EndY=-26.5 EndZ=0
    g10: LineSegment StartX=-10.15 StartY=-12 StartZ=0 EndX=-10.15 EndY=-14 EndZ=0
    g11: LineSegment StartX=-12.8401 StartY=-16 StartZ=0 EndX=-10.1571 EndY=-16 EndZ=0
    g12: LineSegment StartX=-10.15 StartY=-14 StartZ=0 EndX=-8.70761 EndY=-14 EndZ=0
    g13: LineSegment StartX=-12.8401 StartY=-16 StartZ=0 EndX=-12.8401 EndY=-17.6958 EndZ=0
    g14: LineSegment StartX=-10.15 StartY=-12 StartZ=0 EndX=-7.79258 EndY=-12 EndZ=0
    g15: Circle CenterX=-6.2215 CenterY=-2 CenterZ=0 NormalX=0 NormalY=0 NormalZ=1 AngleXU=0 Radius=1
    g16: Circle CenterX=-6.22762 CenterY=-2.58724 CenterZ=0 NormalX=0 NormalY=0 NormalZ=1 AngleXU=0 Radius=1
    g17: Circle CenterX=-6.32538 CenterY=-4 CenterZ=0 NormalX=0 NormalY=0 NormalZ=1 AngleXU=0 Radius=1
    g18: BSplineCurve PolesCount=3 KnotsCount=2 Degree=2 IsPeriodic=0
    g19: GeomPoint X=-6.2215 Y=-2 Z=0
    g20: GeomPoint X=-6.32538 Y=-4 Z=0
    g21: Circle CenterX=-6.48644 CenterY=-5.99526 CenterZ=0 NormalX=0 NormalY=0 NormalZ=1 AngleXU=0 Radius=1
    g22: Circle CenterX=-6.58486 CenterY=-6.99526 CenterZ=0 NormalX=0 NormalY=0 NormalZ=1 AngleXU=0 Radius=1
    g23: Circle CenterX=-6.77343 CenterY=-8 CenterZ=0 NormalX=0 NormalY=0 NormalZ=1 AngleXU=0 Radius=1
    g24: BSplineCurve PolesCount=3 KnotsCount=2 Degree=2 IsPeriodic=0
    g25: GeomPoint X=-6.48644 Y=-5.99526 Z=0
    g26: GeomPoint X=-6.77343 Y=-8 Z=0
    g27: Circle CenterX=-7.19003 CenterY=-10 CenterZ=0 NormalX=0 NormalY=0 NormalZ=1 AngleXU=0 Radius=1
    g28: Circle CenterX=-7.44407 CenterY=-11.0915 CenterZ=0 NormalX=0 NormalY=0 NormalZ=1 AngleXU=0 Radius=1
    g29: Circle CenterX=-7.79258 CenterY=-12 CenterZ=0 NormalX=0 NormalY=0 NormalZ=1 AngleXU=0 Radius=1
    g30: BSplineCurve PolesCount=3 KnotsCount=2 Degree=2 IsPeriodic=0
    g31: GeomPoint X=-7.19003 Y=-10 Z=0
    g32: GeomPoint X=-7.79258 Y=-12 Z=0
    g33: Circle CenterX=-8.70761 CenterY=-14 CenterZ=0 NormalX=0 NormalY=0 NormalZ=1 AngleXU=0 Radius=1
    g34: Circle CenterX=-9.33087 CenterY=-15.1837 CenterZ=0 NormalX=0 NormalY=0 NormalZ=1 AngleXU=0 Radius=1
    g35: Circle CenterX=-10.1571 CenterY=-16 CenterZ=0 NormalX=0 NormalY=0 NormalZ=1 AngleXU=0 Radius=1
    g36: BSplineCurve PolesCount=3 KnotsCount=2 Degree=2 IsPeriodic=0
    g37: GeomPoint X=-8.70761 Y=-14 Z=0
    g38: GeomPoint X=-10.1571 Y=-16 Z=0
    g39: Circle CenterX=-12.8401 CenterY=-17.6958 CenterZ=0 NormalX=0 NormalY=0 NormalZ=1 AngleXU=0 Radius=1
    g40: Circle CenterX=-13.3521 CenterY=-17.9027 CenterZ=0 NormalX=0 NormalY=0 NormalZ=1 AngleXU=0 Radius=1
    g41: Circle CenterX=-14 CenterY=-18 CenterZ=0 NormalX=0 NormalY=0 NormalZ=1 AngleXU=0 Radius=1
    g42: BSplineCurve PolesCount=3 KnotsCount=2 Degree=2 IsPeriodic=0
    g43: GeomPoint X=-12.8401 Y=-17.6958 Z=0
    g44: GeomPoint X=-14 Y=-18 Z=0
    g45: LineSegment StartX=-6.2 StartY=0 StartZ=0 EndX=-7.2 EndY=0 EndZ=0
    g46: LineSegment StartX=-7.2 StartY=0 StartZ=0 EndX=-7.2 EndY=-2 EndZ=0
    g47: LineSegment StartX=-7.2 StartY=-2 StartZ=0 EndX=-6.2215 EndY=-2 EndZ=0
    g48: LineSegment StartX=-6.32538 StartY=-4 StartZ=0 EndX=-7.65538 EndY=-4 EndZ=0
    g49: LineSegment StartX=-7.65538 StartY=-4 StartZ=0 EndX=-7.65538 EndY=-5.99526 EndZ=0
    g50: LineSegment StartX=-7.65538 StartY=-5.99526 StartZ=0 EndX=-6.48644 EndY=-5.99526 EndZ=0
    g51: LineSegment StartX=-6.77343 StartY=-8 StartZ=0 EndX=-8.43343 EndY=-8 EndZ=0
    g52: LineSegment StartX=-8.43343 StartY=-8 StartZ=0 EndX=-8.43343 EndY=-10 EndZ=0
    g53: LineSegment StartX=-8.43343 StartY=-10 StartZ=0 EndX=-7.19003 EndY=-10 EndZ=0
  constraints (112):
    c: Horizontal(g0)
    c: Distance(g0) = 2
    c: Block(g0)
    c: Vertical(g1)
    c: Coincident(g2,g0)
    c: Vertical(g2)
    c: Block(g2)
    c: Coincident(g6,g2)
    c: Weight(g3) = 1
    c: Equal(g3,g4)
    c: Equal(g3,g5)
    c: InternalAlignment(g3,g6)
    c: InternalAlignment(g4,g6)
    c: InternalAlignment(g5,g6)
    c: InternalAlignment(g7,g6)
    c: InternalAlignment(g8,g6)
    c: Block(g6)
    c: Coincident(g9,g1)
    c: Coincident(g9,g6)
    c: Horizontal(g9)
    c: Vertical(g10)
    c: Block(g10)
    c: Horizontal(g11)
    c: Block(g11)
    c: Coincident(g12,g10)
    c: Horizontal(g12)
    c: Block(g12)
    c: Coincident(g13,g11)
    c: Vertical(g13)
    c: Block(g13)
    c: Coincident(g14,g10)
    c: Horizontal(g14)
    c: Block(g14)
    c: Block(g9)
    c: Block(g1)
    c: Weight(g15) = 1
    c: Equal(g15,g16)
    c: Equal(g15,g17)
    c: InternalAlignment(g15,g18)
    c: InternalAlignment(g16,g18)
    c: InternalAlignment(g17,g18)
    c: InternalAlignment(g19,g18)
    c: InternalAlignment(g20,g18)
    c: Weight(g21) = 1
    c: Equal(g21,g22)
    c: Equal(g21,g23)
    c: InternalAlignment(g21,g24)
    c: InternalAlignment(g22,g24)
    c: InternalAlignment(g23,g24)
    c: InternalAlignment(g25,g24)
    c: InternalAlignment(g26,g24)
    c: Weight(g27) = 1
    c: Equal(g27,g28)
    c: Equal(g27,g29)
    c: Coincident(g30,g14)
    c: InternalAlignment(g27,g30)
    c: InternalAlignment(g28,g30)
    c: InternalAlignment(g29,g30)
    c: InternalAlignment(g31,g30)
    c: InternalAlignment(g32,g30)
    c: Coincident(g36,g12)
    c: Weight(g33) = 1
    c: Equal(g33,g34)
    c: Equal(g33,g35)
    c: Coincident(g36,g11)
    c: InternalAlignment(g33,g36)
    c: InternalAlignment(g34,g36)
    c: InternalAlignment(g35,g36)
    c: InternalAlignment(g37,g36)
    c: InternalAlignment(g38,g36)
    c: Coincident(g42,g13)
    c: Weight(g39) = 1
    c: Equal(g39,g40)
    c: Equal(g39,g41)
    c: Coincident(g42,g1)
    c: InternalAlignment(g39,g42)
    c: InternalAlignment(g40,g42)
    c: InternalAlignment(g41,g42)
    c: InternalAlignment(g43,g42)
    c: InternalAlignment(g44,g42)
    c: Block(g18)
    c: Block(g24)
    c: Block(g30)
    c: Block(g36)
    c: Block(g42)
    c: Horizontal(g45)
    c: Coincident(g45,g0)
    c: Vertical(g46)
    c: Coincident(g46,g45)
    c: Coincident(g47,g46)
    c: Coincident(g47,g18)
    c: Horizontal(g47)
    c: Block(g46)
    c: Coincident(g48,g18)
    c: Horizontal(g48)
    c: Distance(g48) = 1.33
    c: Vertical(g49)
    c: Coincident(g49,g48)
    c: Coincident(g50,g49)
    c: Coincident(g50,g24)
    c: Horizontal(g50)
    c: Tangent(g50,g22)
    c: Horizontal(g51)
    c: Coincident(g51,g24)
    c: Block(g51)
    c: Vertical(g52)
    c: Block(g52)
    c: Coincident(g52,g51)
    c: Coincident(g53,g52)
    c: Coincident(g53,g30)
    c: Horizontal(g53)
    c: Distance(g1) = 8.5
FEATURE [Part::Feature] Face024
  shape: bbox 9.8 x 26.5 x 2e-07 mm, 1 faces, 0 solids (baked)
FEATURE [Part::Revolution] Revolve024
  Angle = 360
  Axis = (0,1,0)
  Base = (0,0,0)
  FaceMakerClass = Part::FaceMakerBullseye
  Placement = pos=(0,0,0) rot=(0,0,1;1.5708rad)
  Solid = false
  Source = -> Face024
  Symmetric = false
FEATURE [Part::Feature] Face025
  shape: bbox 9.8 x 26.5 x 2e-07 mm, 1 faces, 0 solids (baked)
FEATURE [Part::Revolution] Revolve025
  Angle = 360
  Axis = (0,1,0)
  Base = (0,0,0)
  FaceMakerClass = Part::FaceMakerBullseye
  Placement = pos=(0,0,0) rot=(0,0,1;1.5708rad)
  Solid = false
  Source = -> Face025
  Symmetric = false
FEATURE [Part::MultiFuse] Fusion033
  Placement = pos=(-18,19,36) rot=(0,0,1;0rad)
  Shapes = -> [Revolve025,Revolve024]
FEATURE [Part::Cylinder] Cylinder014
  Angle = 360
  AttacherType = Attacher::AttachEngine3D
  Height = 20
  Placement = pos=(0,0,36.15) rot=(0,0,1;0rad)
  Radius = 14.3
FEATURE [Part::Cylinder] Cylinder015
  Angle = 360
  AttacherType = Attacher::AttachEngine3D
  Height = 10
  Placement = pos=(0,0,36.15) rot=(0,0,1;0rad)
  Radius = 4
FEATURE [Part::MultiFuse] Fusion034  label="removeToCreteHoleForPlugHousing004"
  Placement = pos=(-42,19,36) rot=(0,1,0;1.5708rad)
  Shapes = -> [Cylinder014,Cylinder015]
FEATURE [Part::Cut] Cut008  label="top004"
  Base = -> Cut004
  Placement = pos=(-1,0,0) rot=(0,0,1;0rad)
  Tool = -> Fusion034
FEATURE [Part::Box] Box005  label="Cube005"
  AttacherType = Attacher::AttachEngine3D
  Height = 28
  Length = 3
  Placement = pos=(110.7,19,22) rot=(0,0,1;0rad)
  Width = 15.7
FEATURE [Part::Cylinder] Cylinder016
  Angle = 360
  AttacherType = Attacher::AttachEngine3D
  Height = 10
  Placement = pos=(0,0,36.15) rot=(0,0,1;0rad)
  Radius = 4
FEATURE [Part::Cylinder] Cylinder017
  Angle = 360
  AttacherType = Attacher::AttachEngine3D
  Height = 20
  Placement = pos=(0,0,36.15) rot=(0,0,1;0rad)
  Radius = 10.3
FEATURE [Part::MultiFuse] Fusion035  label="removeToCreteHoleForPlugHousing005"
  Placement = pos=(70,19,36) rot=(0,1,0;1.5708rad)
  Shapes = -> [Cylinder017,Cylinder016]
FEATURE [Part::Cut] Cut009  label="plugHousingTab001"
  Base = -> Box005
  Placement = pos=(-107.4,-14,0) rot=(0,0,1;0rad)
  Tool = -> Fusion035
FEATURE [Part::Box] Box006  label="Cube006"
  AttacherType = Attacher::AttachEngine3D
  Height = 28
  Length = 3
  Placement = pos=(110.7,19,22) rot=(0,0,1;0rad)
  Width = 15.7
FEATURE [Part::Cylinder] Cylinder018
  Angle = 360
  AttacherType = Attacher::AttachEngine3D
  Height = 10
  Placement = pos=(0,0,36.15) rot=(0,0,1;0rad)
  Radius = 4
FEATURE [Part::Cylinder] Cylinder019
  Angle = 360
  AttacherType = Attacher::AttachEngine3D
  Height = 20
  Placement = pos=(0,0,36.15) rot=(0,0,1;0rad)
  Radius = 10.3
FEATURE [Part::MultiFuse] Fusion036  label="removeToCreteHoleForPlugHousing006"
  Placement = pos=(70,19,36) rot=(0,1,0;1.5708rad)
  Shapes = -> [Cylinder019,Cylinder018]
FEATURE [Part::Cut] Cut010  label="plugHousingTab002"
  Base = -> Box006
  Placement = pos=(-107.4,-14,0) rot=(0,0,1;0rad)
  Tool = -> Fusion036
FEATURE [Part::MultiFuse] Fusion037
  Placement = pos=(9.6,23,0) rot=(0,0,1;3.14159rad)
  Shapes = -> [Cut009,Cut010]
FEATURE [Part::Box] Box  label="Cube"
  AttacherType = Attacher::AttachEngine3D
  Height = 10
  Length = 3
  Placement = pos=(3.3,4,12) rot=(0,0,1;0rad)
  Width = 10
FEATURE [Part::Fillet] Fillet004
  Base = -> Fusion028
  Edges = 1 edges r=2: [Edge25]
FEATURE [Part::Fillet] Fillet005  label="plugHousing046"
  Base = -> Fillet004
  Edges = 1 edges r=2: [Edge8]
FEATURE [Part::Fillet] Fillet006
  Base = -> Box
  Edges = 1 edges r=2: [Edge11]
FEATURE [Part::Box] Box007  label="Cube007"
  AttacherType = Attacher::AttachEngine3D
  Height = 10
  Length = 3
  Placement = pos=(3.3,4,50) rot=(0,0,1;0rad)
  Width = 10
FEATURE [Part::Fillet] Fillet007
  Base = -> Box007
  Edges = 1 edges r=2: [Edge12]
FEATURE [Part::Box] Box008  label="Cube008"
  AttacherType = Attacher::AttachEngine3D
  Height = 28
  Length = 4
  Placement = pos=(5,0,22) rot=(0,0,1;0rad)
  Width = 10
FEATURE [Part::Fillet] Fillet008
  Base = -> Box008
  Edges = 1 edges r=1: [Edge7]
FEATURE [Part::Fillet] Fillet009
  Base = -> Fillet008
  Edges = 1 edges r=2: [Edge5]
FEATURE [Part::Fillet] Fillet010
  Base = -> Fillet009
  Edges = 1 edges r=2: [Edge2]
FEATURE [Sketcher::SketchObject] Sketch009  label="topSketch003"
  FullyConstrained = true
  sketch-geometry (4):
    g0: LineSegment StartX=16.8446 StartY=31.512 StartZ=0 EndX=16.3251 EndY=34.4666 EndZ=0
    g1: ArcOfCircle CenterX=19 CenterY=19.2524 CenterZ=0 NormalX=0 NormalY=0 NormalZ=1 AngleXU=0 Radius=15.4476 StartAngle=1.74483 EndAngle=2.72717
    g2: ArcOfCircle CenterX=19 CenterY=19.2524 CenterZ=0 NormalX=0 NormalY=0 NormalZ=1 AngleXU=0 Radius=12.4476 StartAngle=1.74483 EndAngle=2.73189
    g3: LineSegment StartX=4.86004 StartY=25.4725 StartZ=0 EndX=7.58253 EndY=24.2107 EndZ=0
  constraints (7):
    c: Block(g0)
    c: Coincident(g1,g0)
    c: Coincident(g2,g0)
    c: Coincident(g3,g1)
    c: Coincident(g3,g2)
    c: Block(g1)
    c: Block(g2)
FEATURE [Part::Extrusion] Extrude008
  Base = -> Sketch009
  Dir = (0,0,1)
  DirMode = 2
  FaceMakerClass = Part::FaceMakerBullseye
  LengthFwd = 10
  LengthRev = 0
  Placement = pos=(0,0,31) rot=(0,0,1;0rad)
  Solid = true
  Symmetric = false
FEATURE [Part::Cylinder] Cylinder020
  Angle = 360
  AttacherType = Attacher::AttachEngine3D
  Height = 20
  Placement = pos=(0,0,36.15) rot=(0,0,1;0rad)
  Radius = 8.2
FEATURE [Part::Cylinder] Cylinder021
  Angle = 360
  AttacherType = Attacher::AttachEngine3D
  Height = 10
  Placement = pos=(0,0,36.15) rot=(0,0,1;0rad)
  Radius = 4
FEATURE [Part::MultiFuse] Fusion038  label="removeToCreteHoleForPlugHousing007"
  Placement = pos=(-42,19,36) rot=(0,1,0;1.5708rad)
  Shapes = -> [Cylinder020,Cylinder021]
FEATURE [Part::Cut] Cut011
  Base = -> Extrude008
  Tool = -> Fusion038
FEATURE [Part::Fillet] Fillet011
  Base = -> Cut011
  Edges = 1 edges r=2: [Edge1]
FEATURE [Part::Fillet] Fillet012
  Base = -> Fillet011
  Edges = 1 edges r=2.5: [Edge1]
FEATURE [Part::Fillet] Fillet013
  Base = -> Fillet012
  Edges = 1 edges r=2.5: [Edge2]
FEATURE [Part::Box] Box010  label="Cube010"
  AttacherType = Attacher::AttachEngine3D
  Height = 16
  Length = 8
  Placement = pos=(12.7,31.52,28) rot=(0,0,1;0rad)
  Width = 4
FEATURE [Sketcher::SketchObject] Sketch010  label="topSketch004"
  FullyConstrained = true
  sketch-geometry (4):
    g0: LineSegment StartX=16.8446 StartY=31.512 StartZ=0 EndX=16.3251 EndY=34.4666 EndZ=0
    g1: ArcOfCircle CenterX=19 CenterY=19.2524 CenterZ=0 NormalX=0 NormalY=0 NormalZ=1 AngleXU=0 Radius=15.4476 StartAngle=1.74483 EndAngle=2.72717
    g2: ArcOfCircle CenterX=19 CenterY=19.2524 CenterZ=0 NormalX=0 NormalY=0 NormalZ=1 AngleXU=0 Radius=12.4476 StartAngle=1.74483 EndAngle=2.73189
    g3: LineSegment StartX=4.86004 StartY=25.4725 StartZ=0 EndX=7.58253 EndY=24.2107 EndZ=0
  constraints (7):
    c: Block(g0)
    c: Coincident(g1,g0)
    c: Coincident(g2,g0)
    c: Coincident(g3,g1)
    c: Coincident(g3,g2)
    c: Block(g1)
    c: Block(g2)
FEATURE [Part::Cylinder] Cylinder022
  Angle = 360
  AttacherType = Attacher::AttachEngine3D
  Height = 10
  Placement = pos=(0,0,36.15) rot=(0,0,1;0rad)
  Radius = 4
FEATURE [Sketcher::SketchObject] Sketch011  label="topSketch005"
  FullyConstrained = true
  sketch-geometry (4):
    g0: LineSegment StartX=16.8446 StartY=31.512 StartZ=0 EndX=16.3251 EndY=34.4666 EndZ=0
    g1: ArcOfCircle CenterX=19 CenterY=19.2524 CenterZ=0 NormalX=0 NormalY=0 NormalZ=1 AngleXU=0 Radius=15.4476 StartAngle=1.74483 EndAngle=2.72717
    g2: ArcOfCircle CenterX=19 CenterY=19.2524 CenterZ=0 NormalX=0 NormalY=0 NormalZ=1 AngleXU=0 Radius=12.4476 StartAngle=1.74483 EndAngle=2.73189
    g3: LineSegment StartX=4.86004 StartY=25.4725 StartZ=0 EndX=7.58253 EndY=24.2107 EndZ=0
  constraints (7):
    c: Block(g0)
    c: Coincident(g1,g0)
    c: Coincident(g2,g0)
    c: Coincident(g3,g1)
    c: Coincident(g3,g2)
    c: Block(g1)
    c: Block(g2)
FEATURE [Part::Extrusion] Extrude010
  Base = -> Sketch011
  Dir = (0,0,1)
  DirMode = 2
  FaceMakerClass = Part::FaceMakerBullseye
  LengthFwd = 10.6
  LengthRev = 0
  Placement = pos=(0,0,31) rot=(0,0,1;0rad)
  Solid = true
  Symmetric = false
FEATURE [Part::Cylinder] Cylinder023
  Angle = 360
  AttacherType = Attacher::AttachEngine3D
  Height = 20
  Placement = pos=(0,0,36.15) rot=(0,0,1;0rad)
  Radius = 8.2
FEATURE [Part::MultiFuse] Fusion039  label="removeToCreteHoleForPlugHousing008"
  Placement = pos=(-42,19,36) rot=(0,1,0;1.5708rad)
  Shapes = -> [Cylinder023,Cylinder022]
FEATURE [Part::Cut] Cut012
  Base = -> Extrude010
  Placement = pos=(0,0,-0.3) rot=(0,0,1;0rad)
  Tool = -> Fusion039
FEATURE [Part::Cut] Cut013
  Base = -> Box010
  Tool = -> Cut012
FEATURE [Part::Fillet] Fillet014
  Base = -> Cut013
  Edges = 1 edges r=0.7: [Edge13]
FEATURE [Part::Fillet] Fillet015
  Base = -> Fillet014
  Edges = 1 edges r=0.7: [Edge13]
FEATURE [Part::Fillet] Fillet016
  Base = -> Fillet015
  Edges = 1 edges r=0.7: [Edge16]
FEATURE [Part::Fillet] Fillet017
  Base = -> Fillet016
  Edges = 1 edges r=0.7: [Edge11]
FEATURE [Part::Fillet] Fillet018
  Base = -> Fillet017
  Edges = 1 edges r=0.7: [Edge10]
FEATURE [Part::Fillet] Fillet019
  Base = -> Fillet018
  Edges = 1 edges r=1.2: [Edge5]
FEATURE [Part::Fillet] Fillet020
  Base = -> Fillet019
  Edges = 1 edges r=1.2: [Edge12]
FEATURE [Part::Fillet] Fillet021
  Base = -> Fillet020
  Edges = 1 edges r=2: [Edge1]
  Placement = pos=(0.3,0,0) rot=(0,0,1;0rad)
FEATURE [Part::MultiFuse] Fusion040  label="top005"
  Shapes = -> [Cut008,Fillet021]
FEATURE [Part::MultiFuse] Fusion041  label="wireHolder"
  Shapes = -> [Fusion033,Fillet013]
FEATURE [Part::MultiFuse] Fusion042
  Shapes = -> [Fillet007,Fusion041]
FEATURE [Part::MultiFuse] Fusion043  label="wireHolder001"
  Shapes = -> [Fusion042,Fillet010]
FEATURE [Part::MultiFuse] Fusion044  label="wireHolder002"
  Shapes = -> [Fillet006,Fusion037,Fusion043]
FEATURE [Part::Feature] Face026
  shape: bbox 11 x 6 x 2e-07 mm, 1 faces, 0 solids (baked)
FEATURE [Part::Revolution] Revolve026
  Angle = 360
  Axis = (0,1,0)
  Base = (0,0,0)
  FaceMakerClass = Part::FaceMakerBullseye
  Placement = pos=(30.3,-1,19.7) rot=(0,0,1;0rad)
  Solid = false
  Source = -> Face026
  Symmetric = false
FEATURE [Sketcher::SketchObject] Sketch013  label="topSketch006"
  FullyConstrained = true
  sketch-geometry (13):
    g0: LineSegment StartX=117 StartY=19 StartZ=0 EndX=117 EndY=38 EndZ=0
    g1: ArcOfCircle CenterX=98 CenterY=19 CenterZ=0 NormalX=0 NormalY=0 NormalZ=1 AngleXU=0 Radius=19 StartAngle=5.7297 EndAngle=6.28319
    g2: LineSegment StartX=0 StartY=3 StartZ=0 EndX=0 EndY=19 EndZ=0
    g3: LineSegment StartX=19 StartY=38 StartZ=0 EndX=117 EndY=38 EndZ=0
    g4: ArcOfCircle CenterX=19 CenterY=19 CenterZ=0 NormalX=0 NormalY=0 NormalZ=1 AngleXU=0 Radius=19 StartAngle=1.5708 EndAngle=3.14159
    g5: ArcOfCircle CenterX=19 CenterY=19 CenterZ=0 NormalX=0 NormalY=0 NormalZ=1 AngleXU=0 Radius=16 StartAngle=1.5708 EndAngle=3.14159
    g6: ArcOfCircle CenterX=98 CenterY=19 CenterZ=0 NormalX=0 NormalY=0 NormalZ=1 AngleXU=0 Radius=16 StartAngle=5.60905 EndAngle=6.28319
    g7: LineSegment StartX=114 StartY=19 StartZ=0 EndX=114 EndY=35 EndZ=0
    g8: LineSegment StartX=110.5 StartY=9.01251 StartZ=0 EndX=114.163 EndY=9.01251 EndZ=0
    g9: LineSegment StartX=114 StartY=35 StartZ=0 EndX=19 EndY=35 EndZ=0
    g10: LineSegment StartX=0 StartY=3 StartZ=0 EndX=0 EndY=0 EndZ=0
    g11: LineSegment StartX=3 StartY=0 StartZ=0 EndX=0 EndY=0 EndZ=0
    g12: LineSegment StartX=3 StartY=19 StartZ=0 EndX=3 EndY=0 EndZ=0
  constraints (33):
    c: Vertical(g0)
    c: Distance(g0) = 19
    c: Block(g0)
    c: Coincident(g1,g0)
    c: Block(g1)
    c: Vertical(g2)
    c: Block(g2)
    c: Coincident(g3,g0)
    c: Horizontal(g3)
    c: Distance(g3) = 98
    c: Coincident(g4,g3)
    c: Coincident(g4,g2)
    c: Block(g4)
    c: Coincident(g5,g4)
    c: Coincident(g6,g1)
    c: Block(g6)
    c: Block(g5)
    c: Coincident(g7,g6)
    c: Vertical(g7)
    c: Coincident(g8,g6)
    c: Coincident(g8,g1)
    c: Coincident(g9,g7)
    c: Coincident(g9,g5)
    c: Horizontal(g9)
    c: Tangent(g9,g5)
    c: Coincident(g10,g2)
    c: Distance(g10) = 3
    c: Vertical(g10)
    c: Coincident(g11,g10)
    c: Horizontal(g11)
    c: Coincident(g12,g5)
    c: Coincident(g12,g11)
    c: Vertical(g12)
FEATURE [Part::Extrusion] Extrude011  label="top006"
  Base = -> Sketch013
  Dir = (0,0,1)
  DirMode = 2
  FaceMakerClass = Part::FaceMakerBullseye
  LengthFwd = 72
  LengthRev = 0
  Solid = true
  Symmetric = false
FEATURE [Sketcher::SketchObject] Sketch014
  FullyConstrained = true
  MapMode = 3
  Placement = pos=(0,0,0) rot=(1,0,0;1.5708rad)
  Support = -> [Extrude011]
  sketch-geometry (8):
    g0: Circle CenterX=80.351 CenterY=-67.6202 CenterZ=0 NormalX=0 NormalY=0 NormalZ=1 AngleXU=0 Radius=2
    g1: Circle CenterX=80.351 CenterY=-67.6202 CenterZ=0 NormalX=0 NormalY=0 NormalZ=1 AngleXU=0 Radius=3
    g2: Circle CenterX=80.351 CenterY=-4.92017 CenterZ=0 NormalX=0 NormalY=0 NormalZ=1 AngleXU=0 Radius=2
    g3: Circle CenterX=80.351 CenterY=-4.92017 CenterZ=0 NormalX=0 NormalY=0 NormalZ=1 AngleXU=0 Radius=3
    g4: Circle CenterX=23.851 CenterY=-4.92017 CenterZ=0 NormalX=0 NormalY=0 NormalZ=1 AngleXU=0 Radius=2
    g5: Circle CenterX=23.851 CenterY=-4.92017 CenterZ=0 NormalX=0 NormalY=0 NormalZ=1 AngleXU=0 Radius=3
    g6: Circle CenterX=23.851 CenterY=-67.6202 CenterZ=0 NormalX=0 NormalY=0 NormalZ=1 AngleXU=0 Radius=2
    g7: Circle CenterX=23.851 CenterY=-67.6202 CenterZ=0 NormalX=0 NormalY=0 NormalZ=1 AngleXU=0 Radius=3
  constraints (8):
    c: Block(g3)
    c: Block(g2)
    c: Block(g1)
    c: Block(g0)
    c: Block(g6)
    c: Block(g7)
    c: Block(g4)
    c: Block(g5)
FEATURE [Part::Feature] Face027
  shape: bbox 11 x 6 x 2e-07 mm, 1 faces, 0 solids (baked)
FEATURE [Part::Revolution] Revolve027
  Angle = 360
  Axis = (0,1,0)
  Base = (0,0,0)
  FaceMakerClass = Part::FaceMakerBullseye
  Placement = pos=(30.3,-1,51.7) rot=(0,0,1;0rad)
  Solid = false
  Source = -> Face027
  Symmetric = false
FEATURE [Part::Feature] Face028
  shape: bbox 11 x 6 x 2e-07 mm, 1 faces, 0 solids (baked)
FEATURE [Part::Revolution] Revolve028
  Angle = 360
  Axis = (0,1,0)
  Base = (0,0,0)
  FaceMakerClass = Part::FaceMakerBullseye
  Placement = pos=(62.3,-1,19.7) rot=(0,0,1;0rad)
  Solid = false
  Source = -> Face028
  Symmetric = false
FEATURE [Part::Feature] Face029
  shape: bbox 11 x 6 x 2e-07 mm, 1 faces, 0 solids (baked)
FEATURE [Part::Revolution] Revolve029
  Angle = 360
  Axis = (0,1,0)
  Base = (0,0,0)
  FaceMakerClass = Part::FaceMakerBullseye
  Placement = pos=(62.3,-1,51.7) rot=(0,0,1;0rad)
  Solid = false
  Source = -> Face029
  Symmetric = false
FEATURE [Part::Feature] Wire
  shape: bbox 11 x 5.2 x 2e-07 mm, 0 faces, 0 solids (baked)
FEATURE [Part::Revolution] Revolve030
  Angle = 360
  Axis = (0,1,0)
  Base = (0,0,0)
  FaceMakerClass = Part::FaceMakerBullseye
  Placement = pos=(30.3,38,19.7) rot=(0,0,1;0rad)
  Solid = true
  Source = -> Wire
  Symmetric = false
FEATURE [Part::Feature] Wire001
  shape: bbox 11 x 5.2 x 2e-07 mm, 0 faces, 0 solids (baked)
FEATURE [Part::Revolution] Revolve031
  Angle = 360
  Axis = (0,1,0)
  Base = (0,0,0)
  FaceMakerClass = Part::FaceMakerBullseye
  Placement = pos=(30.3,38,51.7) rot=(0,0,1;0rad)
  Solid = true
  Source = -> Wire001
  Symmetric = false
FEATURE [Part::Feature] Wire002
  shape: bbox 11 x 5.2 x 2e-07 mm, 0 faces, 0 solids (baked)
FEATURE [Part::Revolution] Revolve032
  Angle = 360
  Axis = (0,1,0)
  Base = (0,0,0)
  FaceMakerClass = Part::FaceMakerBullseye
  Placement = pos=(62.3,38,51.7) rot=(0,0,1;0rad)
  Solid = true
  Source = -> Wire002
  Symmetric = false
FEATURE [Part::Feature] Wire003
  shape: bbox 11 x 5.2 x 2e-07 mm, 0 faces, 0 solids (baked)
FEATURE [Part::Revolution] Revolve033
  Angle = 360
  Axis = (0,1,0)
  Base = (0,0,0)
  FaceMakerClass = Part::FaceMakerBullseye
  Placement = pos=(62.3,38,19.7) rot=(0,0,1;0rad)
  Solid = true
  Source = -> Wire003
  Symmetric = false
FEATURE [Part::MultiFuse] Fusion045  label="altRandScrewHousing"
  Shapes = -> [Revolve029,Revolve027,Revolve028,Revolve026]
FEATURE [Part::MultiFuse] Fusion046  label="fanScrewHousing"
  Shapes = -> [Revolve033,Revolve032,Revolve031,Revolve030]
FEATURE [Sketcher::SketchObject] Sketch015
  FullyConstrained = true
  sketch-geometry (17):
    g0: Circle CenterX=-3.5 CenterY=23.5 CenterZ=0 NormalX=0 NormalY=0 NormalZ=1 AngleXU=0 Radius=1
    g1: Circle CenterX=-1 CenterY=15.25 CenterZ=0 NormalX=0 NormalY=0 NormalZ=1 AngleXU=0 Radius=1
    g2: Circle CenterX=-3.5 CenterY=7 CenterZ=0 NormalX=0 NormalY=0 NormalZ=1 AngleXU=0 Radius=1
    g3: BSplineCurve PolesCount=3 KnotsCount=2 Degree=2 IsPeriodic=0
    g4: GeomPoint X=-3.5 Y=23.5 Z=0
    g5: GeomPoint X=-3.5 Y=7 Z=0
    g6: Circle CenterX=-4.8 CenterY=30.5 CenterZ=0 NormalX=0 NormalY=0 NormalZ=1 AngleXU=0 Radius=1
    g7: Circle CenterX=-3.5 CenterY=30.5 CenterZ=0 NormalX=0 NormalY=0 NormalZ=1 AngleXU=0 Radius=1
    g8: Circle CenterX=-3.5 CenterY=29.2 CenterZ=0 NormalX=0 NormalY=0 NormalZ=1 AngleXU=0 Radius=1
    g9: BSplineCurve PolesCount=3 KnotsCount=2 Degree=2 IsPeriodic=0
    g10: GeomPoint X=-4.8 Y=30.5 Z=0
    g11: GeomPoint X=-3.5 Y=29.2 Z=0
    g12: LineSegment StartX=-3.5 StartY=29.2 StartZ=0 EndX=-3.5 EndY=23.5 EndZ=0
    g13: LineSegment StartX=-4.8 StartY=30.5 StartZ=0 EndX=0 EndY=30.5 EndZ=0
    g14: LineSegment StartX=-3.5 StartY=0.3 StartZ=0 EndX=0 EndY=0.3 EndZ=0
    g15: LineSegment StartX=-3.5 StartY=0.3 StartZ=0 EndX=-3.5 EndY=7 EndZ=0
    g16: LineSegment StartX=0 StartY=0.3 StartZ=0 EndX=0 EndY=30.5 EndZ=0
  constraints (33):
    c: Weight(g0) = 1
    c: Equal(g0,g1)
    c: Equal(g0,g2)
    c: InternalAlignment(g0,g3)
    c: InternalAlignment(g1,g3)
    c: InternalAlignment(g2,g3)
    c: InternalAlignment(g4,g3)
    c: InternalAlignment(g5,g3)
    c: Block(g3)
    c: Weight(g6) = 1
    c: Equal(g6,g7)
    c: Equal(g6,g8)
    c: InternalAlignment(g6,g9)
    c: InternalAlignment(g7,g9)
    c: InternalAlignment(g8,g9)
    c: InternalAlignment(g10,g9)
    c: InternalAlignment(g11,g9)
    c: Block(g9)
    c: Coincident(g12,g9)
    c: Coincident(g12,g3)
    c: Vertical(g12)
    c: Coincident(g13,g9)
    c: Horizontal(g13)
    c: Distance(g13) = 4.8
    c: Horizontal(g14)
    c: Block(g14)
    c: Coincident(g15,g14)
    c: Coincident(g15,g3)
    c: Vertical(g15)
    c: Coincident(g16,g14)
    c: Coincident(g16,g13)
    c: Vertical(g16)
    c: Tangent(g16,g1)
FEATURE [Sketcher::SketchObject] Sketch016
  FullyConstrained = true
  sketch-geometry (16):
    g0: Circle CenterX=-3.5 CenterY=23.5 CenterZ=0 NormalX=0 NormalY=0 NormalZ=1 AngleXU=0 Radius=1
    g1: Circle CenterX=-1 CenterY=15.25 CenterZ=0 NormalX=0 NormalY=0 NormalZ=1 AngleXU=0 Radius=1
    g2: Circle CenterX=-3.5 CenterY=7 CenterZ=0 NormalX=0 NormalY=0 NormalZ=1 AngleXU=0 Radius=1
    g3: BSplineCurve PolesCount=3 KnotsCount=2 Degree=2 IsPeriodic=0
    g4: GeomPoint X=-3.5 Y=23.5 Z=0
    g5: GeomPoint X=-3.5 Y=7 Z=0
    g6: LineSegment StartX=-3.5 StartY=28.2 StartZ=0 EndX=-3.5 EndY=23.5 EndZ=0
    g7: LineSegment StartX=0 StartY=29.5 StartZ=0 EndX=0 EndY=30 EndZ=0
    g8: LineSegment StartX=-3.5 StartY=28.2 StartZ=0 EndX=-3.5 EndY=30 EndZ=0
    g9: LineSegment StartX=0 StartY=30 StartZ=0 EndX=0 EndY=30.5 EndZ=0
    g10: LineSegment StartX=0 StartY=30.5 StartZ=0 EndX=-3.5 EndY=30.5 EndZ=0
    g11: LineSegment StartX=-3.5 StartY=30.5 StartZ=0 EndX=-3.5 EndY=30 EndZ=0
    g12: LineSegment StartX=0 StartY=29.5 StartZ=0 EndX=0 EndY=5 EndZ=0
    g13: LineSegment StartX=-3.5 StartY=0.3 StartZ=0 EndX=-3.5 EndY=7 EndZ=0
    g14: LineSegment StartX=-3.5 StartY=0.3 StartZ=0 EndX=0 EndY=0.3 EndZ=0
    g15: LineSegment StartX=0 StartY=5 StartZ=0 EndX=0 EndY=0.3 EndZ=0
  constraints (39):
    c: Weight(g0) = 1
    c: Equal(g0,g1)
    c: Equal(g0,g2)
    c: InternalAlignment(g0,g3)
    c: InternalAlignment(g1,g3)
    c: InternalAlignment(g2,g3)
    c: InternalAlignment(g4,g3)
    c: InternalAlignment(g5,g3)
    c: Block(g3)
    c: Coincident(g6,g3)
    c: Vertical(g6)
    c: Vertical(g7)
    c: Distance(g7) = 0.5
    c: Coincident(g8,g6)
    c: Vertical(g8)
    c: Block(g6)
    c: Block(g7)
    c: Vertical(g9)
    c: Equal(g7,g9) = 0.5
    c: Block(g9)
    c: Coincident(g9,g7)
    c: Horizontal(g10)
    c: Coincident(g10,g9)
    c: Coincident(g11,g10)
    c: Coincident(g11,g8)
    c: Vertical(g11)
    c: Block(g11)
    c: Coincident(g12,g7)
    c: Vertical(g12)
    c: Coincident(g13,g3)
    c: Vertical(g13)
    c: Distance(g13) = 6.7
    c: Coincident(g14,g13)
    c: Horizontal(g14)
    c: Block(g14)
    c: Coincident(g15,g12)
    c: Coincident(g15,g14)
    c: Vertical(g15)
    c: Block(g15)
FEATURE [Sketcher::SketchObject] Sketch017
  FullyConstrained = true
  sketch-geometry (11):
    g0: LineSegment StartX=-3.5 StartY=1e-16 StartZ=0 EndX=-1.6 EndY=1e-16 EndZ=0
    g1: LineSegment StartX=-1.6 StartY=1e-16 StartZ=0 EndX=-1.6 EndY=1.5 EndZ=0
    g2: LineSegment StartX=-3.5 StartY=1.5 StartZ=0 EndX=-1.6 EndY=1.5 EndZ=0
    g3: LineSegment StartX=-3.5 StartY=1e-16 StartZ=0 EndX=-4.8 EndY=1e-16 EndZ=0
    g4: Circle CenterX=-3.5 CenterY=1.3 CenterZ=0 NormalX=0 NormalY=0 NormalZ=1 AngleXU=0 Radius=1
    g5: Circle CenterX=-3.5 CenterY=1e-16 CenterZ=0 NormalX=0 NormalY=0 NormalZ=1 AngleXU=0 Radius=1
    g6: Circle CenterX=-4.8 CenterY=1e-16 CenterZ=0 NormalX=0 NormalY=0 NormalZ=1 AngleXU=0 Radius=1
    g7: BSplineCurve PolesCount=3 KnotsCount=2 Degree=2 IsPeriodic=0
    g8: GeomPoint X=-3.5 Y=1.3 Z=0
    g9: GeomPoint X=-4.8 Y=1e-16 Z=0
    g10: LineSegment StartX=-3.5 StartY=1.3 StartZ=0 EndX=-3.5 EndY=1.5 EndZ=0
  constraints (24):
    c: Horizontal(g0)
    c: Distance(g0) = 1.9
    c: Block(g0)
    c: Coincident(g1,g0)
    c: Vertical(g1)
    c: Coincident(g2,g1)
    c: Horizontal(g2)
    c: Coincident(g3,g0)
    c: Horizontal(g3)
    c: Distance(g3) = 1.3
    c: Weight(g4) = 1
    c: Equal(g4,g5)
    c: Coincident(g5,g0)
    c: Equal(g4,g6)
    c: Coincident(g7,g3)
    c: InternalAlignment(g4,g7)
    c: InternalAlignment(g5,g7)
    c: InternalAlignment(g6,g7)
    c: InternalAlignment(g8,g7)
    c: InternalAlignment(g9,g7)
    c: Coincident(g10,g7)
    c: Coincident(g10,g2)
    c: Vertical(g10)
    c: Block(g10)
FEATURE [Part::Feature] Face035
  shape: bbox 3.2 x 1.5 x 2e-07 mm, 1 faces, 0 solids (baked)
FEATURE [Part::Revolution] Revolve039  label="backCaseScrewRetainer"
  Angle = 360
  Axis = (0,1,0)
  Base = (0,0,0)
  FaceMakerClass = Part::FaceMakerBullseye
  Placement = pos=(12.5,3,62) rot=(0,0,1;0rad)
  Solid = false
  Source = -> Face035
  Symmetric = false
FEATURE [Part::Feature] Face036
  shape: bbox 3.2 x 1.5 x 2e-07 mm, 1 faces, 0 solids (baked)
FEATURE [Part::Feature] Face039
  shape: bbox 4.8 x 30.2 x 2e-07 mm, 1 faces, 0 solids (baked)
FEATURE [Part::Revolution] Revolve043  label="frontCaseScrewPost002"
  Angle = 360
  Axis = (0,1,0)
  Base = (0,0,0)
  FaceMakerClass = Part::FaceMakerBullseye
  Placement = pos=(89.5,4.5,3.5) rot=(0,0,1;0rad)
  Solid = false
  Source = -> Face039
  Symmetric = false
FEATURE [Part::Feature] Face042
  shape: bbox 4.8 x 30.2 x 2e-07 mm, 1 faces, 0 solids (baked)
FEATURE [Part::Revolution] Revolve046  label="frontCaseScrewPost003"
  Angle = 360
  Axis = (0,1,0)
  Base = (0,0,0)
  FaceMakerClass = Part::FaceMakerBullseye
  Placement = pos=(89.5,4.5,68.5) rot=(0,0,1;0rad)
  Solid = false
  Source = -> Face042
  Symmetric = false
FEATURE [Part::Feature] Face043
  shape: bbox 3.2 x 1.5 x 2e-07 mm, 1 faces, 0 solids (baked)
FEATURE [Part::Revolution] Revolve047  label="frontCaseScrewRetainer002"
  Angle = 360
  Axis = (0,1,0)
  Base = (0,0,0)
  FaceMakerClass = Part::FaceMakerBullseye
  Placement = pos=(89.5,3,68.5) rot=(0,0,1;0rad)
  Solid = false
  Source = -> Face043
  Symmetric = false
FEATURE [Part::Feature] Face044
  shape: bbox 3.2 x 1.5 x 2e-07 mm, 1 faces, 0 solids (baked)
FEATURE [Part::Revolution] Revolve048  label="frontCaseScrewRetainer003"
  Angle = 360
  Axis = (0,1,0)
  Base = (0,0,0)
  FaceMakerClass = Part::FaceMakerBullseye
  Placement = pos=(89.5,3,3.5) rot=(0,0,1;0rad)
  Solid = false
  Source = -> Face044
  Symmetric = false
FEATURE [App::MeasureDistance] Distance002  label="Distance: 1.67 mm"
  Distance = 1.66921
  P1 = (99.2361,4.7524,71.7)
  P2 = (99.2347,6.42161,71.7)
FEATURE [Sketcher::SketchObject] Sketch018
  FullyConstrained = true
  sketch-geometry (7):
    g0: LineSegment StartX=0 StartY=0 StartZ=0 EndX=0 EndY=6 EndZ=0
    g1: Circle CenterX=0 CenterY=0 CenterZ=0 NormalX=0 NormalY=0 NormalZ=1 AngleXU=0 Radius=1
    g2: Circle CenterX=8 CenterY=6 CenterZ=0 NormalX=0 NormalY=0 NormalZ=1 AngleXU=0 Radius=1
    g3: BSplineCurve PolesCount=3 KnotsCount=2 Degree=2 IsPeriodic=0
    g4: GeomPoint X=0 Y=0 Z=0
    g5: GeomPoint X=8 Y=6 Z=0
    g6: LineSegment StartX=0 StartY=6 StartZ=0 EndX=8 EndY=6 EndZ=0
  constraints (14):
    c: Coincident(g0,g-1)
    c: Distance(g0) = 6
    c: Vertical(g0)
    c: Coincident(g3,g0)
    c: Weight(g1) = 1
    c: Equal(g1,g2)
    c: InternalAlignment(g1,g3)
    c: InternalAlignment(g2,g3)
    c: InternalAlignment(g4,g3)
    c: InternalAlignment(g5,g3)
    c: Block(g3)
    c: Coincident(g6,g0)
    c: Coincident(g6,g3)
    c: Horizontal(g6)
FEATURE [Part::Extrusion] Extrude012  label="caseScrewPillarBracket"
  Base = -> Sketch018
  Dir = (0,0,1)
  DirMode = 2
  FaceMakerClass = Part::FaceMakerBullseye
  LengthFwd = 2.4
  LengthRev = 0
  Placement = pos=(15.76,29,8.8) rot=(0,1,0;0rad)
  Solid = true
  Symmetric = false
FEATURE [Sketcher::SketchObject] Sketch019
  FullyConstrained = true
  sketch-geometry (7):
    g0: LineSegment StartX=0 StartY=0 StartZ=0 EndX=0 EndY=6 EndZ=0
    g1: Circle CenterX=0 CenterY=0 CenterZ=0 NormalX=0 NormalY=0 NormalZ=1 AngleXU=0 Radius=1
    g2: Circle CenterX=8 CenterY=6 CenterZ=0 NormalX=0 NormalY=0 NormalZ=1 AngleXU=0 Radius=1
    g3: BSplineCurve PolesCount=3 KnotsCount=2 Degree=2 IsPeriodic=0
    g4: GeomPoint X=0 Y=0 Z=0
    g5: GeomPoint X=8 Y=6 Z=0
    g6: LineSegment StartX=0 StartY=6 StartZ=0 EndX=8 EndY=6 EndZ=0
  constraints (14):
    c: Coincident(g0,g-1)
    c: Distance(g0) = 6
    c: Vertical(g0)
    c: Coincident(g3,g0)
    c: Weight(g1) = 1
    c: Equal(g1,g2)
    c: InternalAlignment(g1,g3)
    c: InternalAlignment(g2,g3)
    c: InternalAlignment(g4,g3)
    c: InternalAlignment(g5,g3)
    c: Block(g3)
    c: Coincident(g6,g0)
    c: Coincident(g6,g3)
    c: Horizontal(g6)
FEATURE [Part::Extrusion] Extrude013  label="caseScrewPillarBracket001"
  Base = -> Sketch019
  Dir = (0,0,1)
  DirMode = 2
  FaceMakerClass = Part::FaceMakerBullseye
  LengthFwd = 2.4
  LengthRev = 0
  Placement = pos=(15.76,29,60.8) rot=(0,0,1;0rad)
  Solid = true
  Symmetric = false
FEATURE [Sketcher::SketchObject] Sketch020
  FullyConstrained = true
  sketch-geometry (7):
    g0: LineSegment StartX=0 StartY=0 StartZ=0 EndX=0 EndY=6 EndZ=0
    g1: Circle CenterX=0 CenterY=0 CenterZ=0 NormalX=0 NormalY=0 NormalZ=1 AngleXU=0 Radius=1
    g2: Circle CenterX=8 CenterY=6 CenterZ=0 NormalX=0 NormalY=0 NormalZ=1 AngleXU=0 Radius=1
    g3: BSplineCurve PolesCount=3 KnotsCount=2 Degree=2 IsPeriodic=0
    g4: GeomPoint X=0 Y=0 Z=0
    g5: GeomPoint X=8 Y=6 Z=0
    g6: LineSegment StartX=0 StartY=6 StartZ=0 EndX=8 EndY=6 EndZ=0
  constraints (14):
    c: Coincident(g0,g-1)
    c: Distance(g0) = 6
    c: Vertical(g0)
    c: Coincident(g3,g0)
    c: Weight(g1) = 1
    c: Equal(g1,g2)
    c: InternalAlignment(g1,g3)
    c: InternalAlignment(g2,g3)
    c: InternalAlignment(g4,g3)
    c: InternalAlignment(g5,g3)
    c: Block(g3)
    c: Coincident(g6,g0)
    c: Coincident(g6,g3)
    c: Horizontal(g6)
FEATURE [Part::Extrusion] Extrude014  label="caseScrewPillarBracket002"
  Base = -> Sketch020
  Dir = (0,0,1)
  DirMode = 2
  FaceMakerClass = Part::FaceMakerBullseye
  LengthFwd = 2.4
  LengthRev = 0
  Placement = pos=(13.7,29,13.26) rot=(0,1,0;-1.5708rad)
  Solid = true
  Symmetric = false
FEATURE [Sketcher::SketchObject] Sketch021
  FullyConstrained = true
  sketch-geometry (7):
    g0: LineSegment StartX=0 StartY=0 StartZ=0 EndX=0 EndY=6 EndZ=0
    g1: Circle CenterX=0 CenterY=0 CenterZ=0 NormalX=0 NormalY=0 NormalZ=1 AngleXU=0 Radius=1
    g2: Circle CenterX=8 CenterY=6 CenterZ=0 NormalX=0 NormalY=0 NormalZ=1 AngleXU=0 Radius=1
    g3: BSplineCurve PolesCount=3 KnotsCount=2 Degree=2 IsPeriodic=0
    g4: GeomPoint X=0 Y=0 Z=0
    g5: GeomPoint X=8 Y=6 Z=0
    g6: LineSegment StartX=0 StartY=6 StartZ=0 EndX=8 EndY=6 EndZ=0
  constraints (14):
    c: Coincident(g0,g-1)
    c: Distance(g0) = 6
    c: Vertical(g0)
    c: Coincident(g3,g0)
    c: Weight(g1) = 1
    c: Equal(g1,g2)
    c: InternalAlignment(g1,g3)
    c: InternalAlignment(g2,g3)
    c: InternalAlignment(g4,g3)
    c: InternalAlignment(g5,g3)
    c: Block(g3)
    c: Coincident(g6,g0)
    c: Coincident(g6,g3)
    c: Horizontal(g6)
FEATURE [Part::Extrusion] Extrude015  label="caseScrewPillarBracket003"
  Base = -> Sketch021
  Dir = (0,0,1)
  DirMode = 2
  FaceMakerClass = Part::FaceMakerBullseye
  LengthFwd = 2.4
  LengthRev = 0
  Placement = pos=(11.3,29,58.74) rot=(0,1,0;1.5708rad)
  Solid = true
  Symmetric = false
FEATURE [Sketcher::SketchObject] Sketch022
  FullyConstrained = true
  sketch-geometry (7):
    g0: LineSegment StartX=0 StartY=0 StartZ=0 EndX=0 EndY=6 EndZ=0
    g1: Circle CenterX=0 CenterY=0 CenterZ=0 NormalX=0 NormalY=0 NormalZ=1 AngleXU=0 Radius=1
    g2: Circle CenterX=8 CenterY=6 CenterZ=0 NormalX=0 NormalY=0 NormalZ=1 AngleXU=0 Radius=1
    g3: BSplineCurve PolesCount=3 KnotsCount=2 Degree=2 IsPeriodic=0
    g4: GeomPoint X=0 Y=0 Z=0
    g5: GeomPoint X=8 Y=6 Z=0
    g6: LineSegment StartX=0 StartY=6 StartZ=0 EndX=8 EndY=6 EndZ=0
  constraints (14):
    c: Coincident(g0,g-1)
    c: Distance(g0) = 6
    c: Vertical(g0)
    c: Coincident(g3,g0)
    c: Weight(g1) = 1
    c: Equal(g1,g2)
    c: InternalAlignment(g1,g3)
    c: InternalAlignment(g2,g3)
    c: InternalAlignment(g4,g3)
    c: InternalAlignment(g5,g3)
    c: Block(g3)
    c: Coincident(g6,g0)
    c: Coincident(g6,g3)
    c: Horizontal(g6)
FEATURE [Part::Extrusion] Extrude016  label="caseScrewPillarBracket004"
  Base = -> Sketch022
  Dir = (0,0,1)
  DirMode = 2
  FaceMakerClass = Part::FaceMakerBullseye
  LengthFwd = 2.4
  LengthRev = 0
  Placement = pos=(88.3,29,65.23) rot=(0,1,0;1.5708rad)
  Solid = true
  Symmetric = false
FEATURE [Sketcher::SketchObject] Sketch023
  FullyConstrained = true
  sketch-geometry (7):
    g0: LineSegment StartX=0 StartY=0 StartZ=0 EndX=0 EndY=6 EndZ=0
    g1: Circle CenterX=0 CenterY=0 CenterZ=0 NormalX=0 NormalY=0 NormalZ=1 AngleXU=0 Radius=1
    g2: Circle CenterX=8 CenterY=6 CenterZ=0 NormalX=0 NormalY=0 NormalZ=1 AngleXU=0 Radius=1
    g3: BSplineCurve PolesCount=3 KnotsCount=2 Degree=2 IsPeriodic=0
    g4: GeomPoint X=0 Y=0 Z=0
    g5: GeomPoint X=8 Y=6 Z=0
    g6: LineSegment StartX=0 StartY=6 StartZ=0 EndX=8 EndY=6 EndZ=0
  constraints (14):
    c: Coincident(g0,g-1)
    c: Distance(g0) = 6
    c: Vertical(g0)
    c: Coincident(g3,g0)
    c: Weight(g1) = 1
    c: Equal(g1,g2)
    c: InternalAlignment(g1,g3)
    c: InternalAlignment(g2,g3)
    c: InternalAlignment(g4,g3)
    c: InternalAlignment(g5,g3)
    c: Block(g3)
    c: Coincident(g6,g0)
    c: Coincident(g6,g3)
    c: Horizontal(g6)
FEATURE [Part::Extrusion] Extrude017  label="caseScrewPillarBracket005"
  Base = -> Sketch023
  Dir = (0,0,1)
  DirMode = 2
  FaceMakerClass = Part::FaceMakerBullseye
  LengthFwd = 2.4
  LengthRev = 0
  Placement = pos=(90.7,29,6.77) rot=(0,-1,0;1.5708rad)
  Solid = true
  Symmetric = false
FEATURE [Sketcher::SketchObject] Sketch024
  FullyConstrained = true
  sketch-geometry (7):
    g0: LineSegment StartX=0 StartY=0 StartZ=0 EndX=0 EndY=6 EndZ=0
    g1: Circle CenterX=0 CenterY=0 CenterZ=0 NormalX=0 NormalY=0 NormalZ=1 AngleXU=0 Radius=1
    g2: Circle CenterX=8 CenterY=6 CenterZ=0 NormalX=0 NormalY=0 NormalZ=1 AngleXU=0 Radius=1
    g3: BSplineCurve PolesCount=3 KnotsCount=2 Degree=2 IsPeriodic=0
    g4: GeomPoint X=0 Y=0 Z=0
    g5: GeomPoint X=8 Y=6 Z=0
    g6: LineSegment StartX=0 StartY=6 StartZ=0 EndX=8 EndY=6 EndZ=0
  constraints (14):
    c: Coincident(g0,g-1)
    c: Distance(g0) = 6
    c: Vertical(g0)
    c: Coincident(g3,g0)
    c: Weight(g1) = 1
    c: Equal(g1,g2)
    c: InternalAlignment(g1,g3)
    c: InternalAlignment(g2,g3)
    c: InternalAlignment(g4,g3)
    c: InternalAlignment(g5,g3)
    c: Block(g3)
    c: Coincident(g6,g0)
    c: Coincident(g6,g3)
    c: Horizontal(g6)
FEATURE [Part::Extrusion] Extrude018  label="caseScrewPillarBracket006"
  Base = -> Sketch024
  Dir = (0,0,1)
  DirMode = 2
  FaceMakerClass = Part::FaceMakerBullseye
  LengthFwd = 2.4
  LengthRev = 0
  Placement = pos=(103.7,29,6.77) rot=(0,-1,0;1.5708rad)
  Solid = true
  Symmetric = false
FEATURE [Sketcher::SketchObject] Sketch025
  FullyConstrained = true
  sketch-geometry (7):
    g0: LineSegment StartX=0 StartY=0 StartZ=0 EndX=0 EndY=6 EndZ=0
    g1: Circle CenterX=0 CenterY=0 CenterZ=0 NormalX=0 NormalY=0 NormalZ=1 AngleXU=0 Radius=1
    g2: Circle CenterX=8 CenterY=6 CenterZ=0 NormalX=0 NormalY=0 NormalZ=1 AngleXU=0 Radius=1
    g3: BSplineCurve PolesCount=3 KnotsCount=2 Degree=2 IsPeriodic=0
    g4: GeomPoint X=0 Y=0 Z=0
    g5: GeomPoint X=8 Y=6 Z=0
    g6: LineSegment StartX=0 StartY=6 StartZ=0 EndX=8 EndY=6 EndZ=0
  constraints (14):
    c: Coincident(g0,g-1)
    c: Distance(g0) = 6
    c: Vertical(g0)
    c: Coincident(g3,g0)
    c: Weight(g1) = 1
    c: Equal(g1,g2)
    c: InternalAlignment(g1,g3)
    c: InternalAlignment(g2,g3)
    c: InternalAlignment(g4,g3)
    c: InternalAlignment(g5,g3)
    c: Block(g3)
    c: Coincident(g6,g0)
    c: Coincident(g6,g3)
    c: Horizontal(g6)
FEATURE [Part::Extrusion] Extrude019  label="caseScrewPillarBracket007"
  Base = -> Sketch025
  Dir = (0,0,1)
  DirMode = 2
  FaceMakerClass = Part::FaceMakerBullseye
  LengthFwd = 2.4
  LengthRev = 0
  Placement = pos=(101.3,29,65.23) rot=(0,1,0;1.5708rad)
  Solid = true
  Symmetric = false
FEATURE [Part::Box] Box011  label="frontCaseScrewPillarBracket"
  AttacherType = Attacher::AttachEngine3D
  Height = 2.4
  Length = 16
  Placement = pos=(87,28,2.3) rot=(0,0,1;0rad)
  Width = 7
FEATURE [Part::Box] Box012  label="frontCaseScrewPillarBracket001"
  AttacherType = Attacher::AttachEngine3D
  Height = 2.4
  Length = 16
  Placement = pos=(87,28,67.3) rot=(0,0,1;0rad)
  Width = 7
FEATURE [Sketcher::SketchObject] Sketch026
  FullyConstrained = true
  sketch-geometry (17):
    g0: Circle CenterX=-3.5 CenterY=23.5 CenterZ=0 NormalX=0 NormalY=0 NormalZ=1 AngleXU=0 Radius=1
    g1: Circle CenterX=-1 CenterY=15.25 CenterZ=0 NormalX=0 NormalY=0 NormalZ=1 AngleXU=0 Radius=1
    g2: Circle CenterX=-3.5 CenterY=7 CenterZ=0 NormalX=0 NormalY=0 NormalZ=1 AngleXU=0 Radius=1
    g3: BSplineCurve PolesCount=3 KnotsCount=2 Degree=2 IsPeriodic=0
    g4: GeomPoint X=-3.5 Y=23.5 Z=0
    g5: GeomPoint X=-3.5 Y=7 Z=0
    g6: Circle CenterX=-4.8 CenterY=30.5 CenterZ=0 NormalX=0 NormalY=0 NormalZ=1 AngleXU=0 Radius=1
    g7: Circle CenterX=-3.5 CenterY=30.5 CenterZ=0 NormalX=0 NormalY=0 NormalZ=1 AngleXU=0 Radius=1
    g8: Circle CenterX=-3.5 CenterY=29.2 CenterZ=0 NormalX=0 NormalY=0 NormalZ=1 AngleXU=0 Radius=1
    g9: BSplineCurve PolesCount=3 KnotsCount=2 Degree=2 IsPeriodic=0
    g10: GeomPoint X=-4.8 Y=30.5 Z=0
    g11: GeomPoint X=-3.5 Y=29.2 Z=0
    g12: LineSegment StartX=-3.5 StartY=29.2 StartZ=0 EndX=-3.5 EndY=23.5 EndZ=0
    g13: LineSegment StartX=-4.8 StartY=30.5 StartZ=0 EndX=0 EndY=30.5 EndZ=0
    g14: LineSegment StartX=-3.5 StartY=5 StartZ=0 EndX=-3.5 EndY=7 EndZ=0
    g15: LineSegment StartX=0 StartY=5 StartZ=0 EndX=0 EndY=30.5 EndZ=0
    g16: LineSegment StartX=-3.5 StartY=5 StartZ=0 EndX=0 EndY=5 EndZ=0
  constraints (33):
    c: Weight(g0) = 1
    c: Equal(g0,g1)
    c: Equal(g0,g2)
    c: InternalAlignment(g0,g3)
    c: InternalAlignment(g1,g3)
    c: InternalAlignment(g2,g3)
    c: InternalAlignment(g4,g3)
    c: InternalAlignment(g5,g3)
    c: Block(g3)
    c: Weight(g6) = 1
    c: Equal(g6,g7)
    c: Equal(g6,g8)
    c: InternalAlignment(g6,g9)
    c: InternalAlignment(g7,g9)
    c: InternalAlignment(g8,g9)
    c: InternalAlignment(g10,g9)
    c: InternalAlignment(g11,g9)
    c: Block(g9)
    c: Coincident(g12,g9)
    c: Coincident(g12,g3)
    c: Vertical(g12)
    c: Coincident(g13,g9)
    c: Horizontal(g13)
    c: Distance(g13) = 4.8
    c: Coincident(g14,g3)
    c: Vertical(g14)
    c: Coincident(g15,g13)
    c: Vertical(g15)
    c: Tangent(g15,g1)
    c: Distance(g14) = 2
    c: Coincident(g16,g14)
    c: Horizontal(g16)
    c: Coincident(g15,g16)
FEATURE [Part::Feature] Face050
  shape: bbox 4.8 x 25.5 x 2e-07 mm, 1 faces, 0 solids (baked)
FEATURE [Part::Revolution] Revolve054  label="moreFrontCaseScrewPost001"
  Angle = 360
  Axis = (0,1,0)
  Base = (0,0,0)
  FaceMakerClass = Part::FaceMakerBullseye
  Placement = pos=(102.5,4.5,3.5) rot=(0,0,1;0rad)
  Solid = false
  Source = -> Face050
  Symmetric = false
FEATURE [Part::Feature] Face051
  shape: bbox 4.8 x 25.5 x 2e-07 mm, 1 faces, 0 solids (baked)
FEATURE [Part::Revolution] Revolve055  label="moreFrontCaseScrewPost002"
  Angle = 360
  Axis = (0,1,0)
  Base = (0,0,0)
  FaceMakerClass = Part::FaceMakerBullseye
  Placement = pos=(102.5,4.5,68.5) rot=(0,0,1;0rad)
  Solid = false
  Source = -> Face051
  Symmetric = false
FEATURE [Sketcher::SketchObject] Sketch027
  FullyConstrained = true
  sketch-geometry (10):
    g0: LineSegment StartX=-1.6 StartY=4.7 StartZ=0 EndX=-1.6 EndY=1.7 EndZ=0
    g1: LineSegment StartX=-3.5 StartY=4.7 StartZ=0 EndX=-1.6 EndY=4.7 EndZ=0
    g2: LineSegment StartX=-1.6 StartY=1.7 StartZ=0 EndX=-1.6 EndY=1.5 EndZ=0
    g3: LineSegment StartX=-1.6 StartY=1.5 StartZ=0 EndX=-5.2 EndY=1.5 EndZ=0
    g4: Circle CenterX=-3.5 CenterY=4.7 CenterZ=0 NormalX=0 NormalY=0 NormalZ=1 AngleXU=0 Radius=1
    g5: Circle CenterX=-3.59627 CenterY=2.99743 CenterZ=0 NormalX=0 NormalY=0 NormalZ=1 AngleXU=0 Radius=1
    g6: Circle CenterX=-5.2 CenterY=1.5 CenterZ=0 NormalX=0 NormalY=0 NormalZ=1 AngleXU=0 Radius=1
    g7: BSplineCurve PolesCount=3 KnotsCount=2 Degree=2 IsPeriodic=0
    g8: GeomPoint X=-3.5 Y=4.7 Z=0
    g9: GeomPoint X=-5.2 Y=1.5 Z=0
  constraints (23):
    c: Vertical(g0)
    c: Distance(g0) = 3
    c: Coincident(g1,g0)
    c: Horizontal(g1)
    c: Block(g0)
    c: Block(g1)
    c: Coincident(g2,g0)
    c: Vertical(g2)
    c: Distance(g2) = 0.2
    c: Coincident(g3,g2)
    c: Horizontal(g3)
    c: Block(g3)
    c: Coincident(g7,g1)
    c: Weight(g4) = 1
    c: Equal(g4,g5)
    c: Equal(g4,g6)
    c: Coincident(g7,g3)
    c: InternalAlignment(g4,g7)
    c: InternalAlignment(g5,g7)
    c: InternalAlignment(g6,g7)
    c: InternalAlignment(g8,g7)
    c: InternalAlignment(g9,g7)
    c: Block(g7)
FEATURE [Sketcher::SketchObject] Sketch028
  FullyConstrained = true
  sketch-geometry (18):
    g0: LineSegment StartX=0 StartY=3e-16 StartZ=0 EndX=0 EndY=1.7 EndZ=0
    g1: LineSegment StartX=-3.5 StartY=0 StartZ=0 EndX=-3.5 EndY=0.9 EndZ=0
    g2: Circle CenterX=-2.7 CenterY=1.7 CenterZ=0 NormalX=0 NormalY=0 NormalZ=1 AngleXU=0 Radius=1
    g3: Circle CenterX=-3.5 CenterY=1.7 CenterZ=0 NormalX=0 NormalY=0 NormalZ=1 AngleXU=0 Radius=1
    g4: Circle CenterX=-3.5 CenterY=0.9 CenterZ=0 NormalX=0 NormalY=0 NormalZ=1 AngleXU=0 Radius=1
    g5: BSplineCurve PolesCount=3 KnotsCount=2 Degree=2 IsPeriodic=0
    g6: GeomPoint X=-2.7 Y=1.7 Z=0
    g7: GeomPoint X=-3.5 Y=0.9 Z=0
    g8: LineSegment StartX=-3.5 StartY=0 StartZ=0 EndX=-3.5 EndY=-7 EndZ=0
    g9: LineSegment StartX=0 StartY=3e-16 StartZ=0 EndX=0 EndY=-7 EndZ=0
    g10: LineSegment StartX=-3.5 StartY=-7 StartZ=0 EndX=0 EndY=-7 EndZ=0
    g11: LineSegment StartX=-2.7 StartY=1.7 StartZ=0 EndX=-1.6 EndY=1.7 EndZ=0
    g12: LineSegment StartX=0 StartY=1.7 StartZ=0 EndX=0 EndY=4.5 EndZ=0
    g13: LineSegment StartX=0 StartY=4.5 StartZ=0 EndX=0 EndY=10.8 EndZ=0
    g14: LineSegment StartX=0 StartY=10.8 StartZ=0 EndX=-2 EndY=10.8 EndZ=0
    g15: LineSegment StartX=-1.6 StartY=4.7 StartZ=0 EndX=-1.6 EndY=1.7 EndZ=0
    g16: LineSegment StartX=-1.6 StartY=4.7 StartZ=0 EndX=-2 EndY=4.7 EndZ=0
    g17: LineSegment StartX=-2 StartY=4.7 StartZ=0 EndX=-2 EndY=10.8 EndZ=0
  constraints (44):
    c: Vertical(g0)
    c: Vertical(g1)
    c: Distance(g1) = 0.9
    c: Block(g0)
    c: Distance(g0) = 1.7
    c: Weight(g2) = 1
    c: Equal(g2,g3)
    c: Equal(g2,g4)
    c: Coincident(g5,g1)
    c: InternalAlignment(g2,g5)
    c: InternalAlignment(g3,g5)
    c: InternalAlignment(g4,g5)
    c: InternalAlignment(g6,g5)
    c: InternalAlignment(g7,g5)
    c: Block(g5)
    c: Coincident(g8,g1)
    c: Vertical(g8)
    c: Distance(g8) = 7
    c: Vertical(g9)
    c: Equal(g8,g9) = 7
    c: Coincident(g9,g0)
    c: Coincident(g10,g8)
    c: Coincident(g10,g9)
    c: Horizontal(g10)
    c: Coincident(g11,g5)
    c: Horizontal(g11)
    c: Coincident(g12,g0)
    c: Vertical(g12)
    c: Distance(g12) = 2.8
    c: Coincident(g13,g12)
    c: Vertical(g13)
    c: Distance(g13) = 6.3
    c: Coincident(g14,g13)
    c: Horizontal(g14)
    c: Distance(g14) = 2
    c: Vertical(g15)
    c: Distance(g15) = 3
    c: Block(g11)
    c: Coincident(g15,g11)
    c: Coincident(g16,g15)
    c: Horizontal(g16)
    c: Coincident(g17,g16)
    c: Coincident(g17,g14)
    c: Vertical(g17)
FEATURE [Part::Revolution] Revolve040  label="backCaseScrewRetainer001"
  Angle = 360
  Axis = (0,1,0)
  Base = (0,0,0)
  FaceMakerClass = Part::FaceMakerBullseye
  Placement = pos=(12.5,3,10) rot=(0,0,1;0rad)
  Solid = false
  Source = -> Face036
  Symmetric = false
FEATURE [Part::Feature] Face055
  shape: bbox 3.5 x 30.2 x 2e-07 mm, 1 faces, 0 solids (baked)
FEATURE [Part::Revolution] Revolve059  label="backCaseScrewPost"
  Angle = 360
  Axis = (0,1,0)
  Base = (0,0,0)
  FaceMakerClass = Part::FaceMakerBullseye
  Placement = pos=(12.5,4.5,10) rot=(0,0,1;0rad)
  Solid = false
  Source = -> Face055
  Symmetric = false
FEATURE [Part::Feature] Face056
  shape: bbox 3.5 x 30.2 x 2e-07 mm, 1 faces, 0 solids (baked)
FEATURE [Part::Revolution] Revolve060  label="backCaseScrewPost001"
  Angle = 360
  Axis = (0,1,0)
  Base = (0,0,0)
  FaceMakerClass = Part::FaceMakerBullseye
  Placement = pos=(12.5,4.5,62) rot=(0,0,1;0rad)
  Solid = false
  Source = -> Face056
  Symmetric = false
FEATURE [Part::Feature] Face057
  shape: bbox 3.5 x 17.8 x 2e-07 mm, 1 faces, 0 solids (baked)
FEATURE [Part::Revolution] Revolve061  label="removeToCreateScrewAndThreadedInsertHole"
  Angle = 360
  Axis = (0,1,0)
  Base = (0,0,0)
  FaceMakerClass = Part::FaceMakerBullseye
  Placement = pos=(12.5,0,10) rot=(0,0,1;0rad)
  Solid = false
  Source = -> Face057
  Symmetric = false
FEATURE [Part::Feature] Face058
  shape: bbox 3.5 x 17.8 x 2e-07 mm, 1 faces, 0 solids (baked)
FEATURE [Part::Revolution] Revolve062  label="removeToCreateScrewAndThreadedInsertHole001"
  Angle = 360
  Axis = (0,1,0)
  Base = (0,0,0)
  FaceMakerClass = Part::FaceMakerBullseye
  Placement = pos=(12.5,0,62) rot=(0,0,1;0rad)
  Solid = false
  Source = -> Face058
  Symmetric = false
FEATURE [Part::Feature] Face059
  shape: bbox 3.5 x 17.8 x 2e-07 mm, 1 faces, 0 solids (baked)
FEATURE [Part::Revolution] Revolve063  label="removeToCreateScrewAndThreadedInsertHole002"
  Angle = 360
  Axis = (0,1,0)
  Base = (0,0,0)
  FaceMakerClass = Part::FaceMakerBullseye
  Placement = pos=(89.5,0,68.5) rot=(0,0,1;0rad)
  Solid = false
  Source = -> Face059
  Symmetric = false
FEATURE [Part::Feature] Face060
  shape: bbox 3.5 x 17.8 x 2e-07 mm, 1 faces, 0 solids (baked)
FEATURE [Part::Revolution] Revolve064  label="removeToCreateScrewAndThreadedInsertHole003"
  Angle = 360
  Axis = (0,1,0)
  Base = (0,0,0)
  FaceMakerClass = Part::FaceMakerBullseye
  Placement = pos=(89.5,0,3.5) rot=(0,0,1;0rad)
  Solid = false
  Source = -> Face060
  Symmetric = false
FEATURE [Part::Feature] Face061
  shape: bbox 3.5 x 17.8 x 2e-07 mm, 1 faces, 0 solids (baked)
FEATURE [Part::Revolution] Revolve065  label="removeToCreateScrewAndThreadedInsertHole004"
  Angle = 360
  Axis = (0,1,0)
  Base = (0,0,0)
  FaceMakerClass = Part::FaceMakerBullseye
  Placement = pos=(102.5,4.7,3.5) rot=(0,0,1;0rad)
  Solid = false
  Source = -> Face061
  Symmetric = false
FEATURE [Part::Feature] Face062
  shape: bbox 3.5 x 17.8 x 2e-07 mm, 1 faces, 0 solids (baked)
FEATURE [Part::Revolution] Revolve066  label="removeToCreateScrewAndThreadedInsertHole005"
  Angle = 360
  Axis = (0,1,0)
  Base = (0,0,0)
  FaceMakerClass = Part::FaceMakerBullseye
  Placement = pos=(102.5,4.7,68.5) rot=(0,0,1;0rad)
  Solid = false
  Source = -> Face062
  Symmetric = false
FEATURE [Part::MultiFuse] Fusion047  label="makeHoles"
  Shapes = -> [Revolve066,Revolve065,Revolve064,Revolve063,Revolve062,Revolve061]
FEATURE [Part::Feature] Face063
  shape: bbox 3.6 x 3.2 x 2e-07 mm, 1 faces, 0 solids (baked)
FEATURE [Part::Revolution] Revolve067  label="moreFrontCaseScrewRetainer002"
  Angle = 360
  Axis = (0,1,0)
  Base = (0,0,0)
  FaceMakerClass = Part::FaceMakerBullseye
  Placement = pos=(102.5,4.5,68.5) rot=(0,0,1;0rad)
  Solid = false
  Source = -> Face063
  Symmetric = false
FEATURE [Part::Feature] Face064
  shape: bbox 3.6 x 3.2 x 2e-07 mm, 1 faces, 0 solids (baked)
FEATURE [Part::Revolution] Revolve068  label="moreFrontCaseScrewRetainer003"
  Angle = 360
  Axis = (0,1,0)
  Base = (0,0,0)
  FaceMakerClass = Part::FaceMakerBullseye
  Placement = pos=(102.5,4.5,3.5) rot=(0,0,1;0rad)
  Solid = false
  Source = -> Face064
  Symmetric = false
FEATURE [Part::Feature] Face065
  shape: bbox 3.5 x 17.8 x 2e-07 mm, 1 faces, 0 solids (baked)
FEATURE [Part::Revolution] Revolve069  label="removeToCreateScrewAndThreadedInsertHole006"
  Angle = 360
  Axis = (0,1,0)
  Base = (0,0,0)
  FaceMakerClass = Part::FaceMakerBullseye
  Placement = pos=(12.5,0,10) rot=(0,0,1;0rad)
  Solid = false
  Source = -> Face065
  Symmetric = false
FEATURE [Part::Feature] Face066
  shape: bbox 3.5 x 17.8 x 2e-07 mm, 1 faces, 0 solids (baked)
FEATURE [Part::Revolution] Revolve070  label="removeToCreateScrewAndThreadedInsertHole007"
  Angle = 360
  Axis = (0,1,0)
  Base = (0,0,0)
  FaceMakerClass = Part::FaceMakerBullseye
  Placement = pos=(12.5,0,62) rot=(0,0,1;0rad)
  Solid = false
  Source = -> Face066
  Symmetric = false
FEATURE [Part::Feature] Face067
  shape: bbox 3.5 x 17.8 x 2e-07 mm, 1 faces, 0 solids (baked)
FEATURE [Part::Revolution] Revolve071  label="removeToCreateScrewAndThreadedInsertHole008"
  Angle = 360
  Axis = (0,1,0)
  Base = (0,0,0)
  FaceMakerClass = Part::FaceMakerBullseye
  Placement = pos=(89.5,0,68.5) rot=(0,0,1;0rad)
  Solid = false
  Source = -> Face067
  Symmetric = false
FEATURE [Part::Feature] Face068
  shape: bbox 3.5 x 17.8 x 2e-07 mm, 1 faces, 0 solids (baked)
FEATURE [Part::Revolution] Revolve072  label="removeToCreateScrewAndThreadedInsertHole009"
  Angle = 360
  Axis = (0,1,0)
  Base = (0,0,0)
  FaceMakerClass = Part::FaceMakerBullseye
  Placement = pos=(89.5,0,3.5) rot=(0,0,1;0rad)
  Solid = false
  Source = -> Face068
  Symmetric = false
FEATURE [Part::Feature] Face069
  shape: bbox 3.5 x 17.8 x 2e-07 mm, 1 faces, 0 solids (baked)
FEATURE [Part::Feature] Face070
  shape: bbox 3.5 x 17.8 x 2e-07 mm, 1 faces, 0 solids (baked)
FEATURE [Part::Revolution] Revolve073  label="removeToCreateScrewAndThreadedInsertHole010"
  Angle = 360
  Axis = (0,1,0)
  Base = (0,0,0)
  FaceMakerClass = Part::FaceMakerBullseye
  Placement = pos=(102.5,4.7,3.5) rot=(0,0,1;0rad)
  Solid = false
  Source = -> Face069
  Symmetric = false
FEATURE [Part::Revolution] Revolve074  label="removeToCreateScrewAndThreadedInsertHole011"
  Angle = 360
  Axis = (0,1,0)
  Base = (0,0,0)
  FaceMakerClass = Part::FaceMakerBullseye
  Placement = pos=(102.5,4.7,68.5) rot=(0,0,1;0rad)
  Solid = false
  Source = -> Face070
  Symmetric = false
FEATURE [Part::MultiFuse] Fusion048  label="makeHoles001"
  Shapes = -> [Revolve074,Revolve073,Revolve072,Revolve071,Revolve070,Revolve069]
FEATURE [Part::MultiFuse] Fusion049  label="caseScrewRetainers"
  Shapes = -> [Revolve067,Revolve068,Revolve048,Revolve047,Revolve039,Revolve040]
FEATURE [Part::Cut] Cut015  label="caseScrewRetainers001"
  Base = -> Fusion049
  Tool = -> Fusion048
FEATURE [Part::MultiFuse] Fusion050  label="casePillars"
  Shapes = -> [Revolve055,Revolve054,Revolve043,Revolve046,Revolve059,Revolve060]
FEATURE [Part::Feature] Face071 .. Face076  x6 (patterned run collapsed; names and placements below)
  shape: bbox 3.5 x 17.8 x 2e-07 mm, 1 faces, 0 solids (baked)
FEATURE [Part::Revolution] Revolve075  label="removeToCreateScrewAndThreadedInsertHole012"
  Angle = 360
  Axis = (0,1,0)
  Base = (0,0,0)
  FaceMakerClass = Part::FaceMakerBullseye
  Placement = pos=(12.5,0,10) rot=(0,0,1;0rad)
  Solid = false
  Source = -> Face071
  Symmetric = false
FEATURE [Part::Revolution] Revolve076  label="removeToCreateScrewAndThreadedInsertHole013"
  Angle = 360
  Axis = (0,1,0)
  Base = (0,0,0)
  FaceMakerClass = Part::FaceMakerBullseye
  Placement = pos=(12.5,0,62) rot=(0,0,1;0rad)
  Solid = false
  Source = -> Face072
  Symmetric = false
FEATURE [Part::Revolution] Revolve077  label="removeToCreateScrewAndThreadedInsertHole014"
  Angle = 360
  Axis = (0,1,0)
  Base = (0,0,0)
  FaceMakerClass = Part::FaceMakerBullseye
  Placement = pos=(89.5,0,68.5) rot=(0,0,1;0rad)
  Solid = false
  Source = -> Face073
  Symmetric = false
FEATURE [Part::Revolution] Revolve078  label="removeToCreateScrewAndThreadedInsertHole015"
  Angle = 360
  Axis = (0,1,0)
  Base = (0,0,0)
  FaceMakerClass = Part::FaceMakerBullseye
  Placement = pos=(89.5,0,3.5) rot=(0,0,1;0rad)
  Solid = false
  Source = -> Face074
  Symmetric = false
FEATURE [Part::Revolution] Revolve079  label="removeToCreateScrewAndThreadedInsertHole016"
  Angle = 360
  Axis = (0,1,0)
  Base = (0,0,0)
  FaceMakerClass = Part::FaceMakerBullseye
  Placement = pos=(102.5,4.7,3.5) rot=(0,0,1;0rad)
  Solid = false
  Source = -> Face075
  Symmetric = false
FEATURE [Part::Revolution] Revolve080  label="removeToCreateScrewAndThreadedInsertHole017"
  Angle = 360
  Axis = (0,1,0)
  Base = (0,0,0)
  FaceMakerClass = Part::FaceMakerBullseye
  Placement = pos=(102.5,4.7,68.5) rot=(0,0,1;0rad)
  Solid = false
  Source = -> Face076
  Symmetric = false
FEATURE [Part::MultiFuse] Fusion051  label="makeHoles002"
  Shapes = -> [Revolve080,Revolve079,Revolve078,Revolve077,Revolve076,Revolve075]
FEATURE [Part::Cut] Cut016  label="caesPillars"
  Base = -> Fusion050
  Tool = -> Fusion051
FEATURE [Part::Revolution] Revolve009  label="plugHousing016"
  Angle = 360
  Axis = (0,1,0)
  Base = (0,0,0)
  FaceMakerClass = Part::FaceMakerBullseye
  Placement = pos=(0,0,36.15) rot=(0,0,1;0rad)
  Solid = false
  Source = -> Face012
  Symmetric = false
FEATURE [Part::MultiFuse] Fusion014  label="plugHousing023"
  Placement = pos=(0,0,0) rot=(0,0,1;1.5708rad)
  Shapes = -> [Revolve011,Revolve009]
FEATURE [Part::Revolution] Revolve010  label="plugHousing017"
  Angle = 360
  Axis = (0,1,0)
  Base = (0,0,0)
  FaceMakerClass = Part::FaceMakerBullseye
  Placement = pos=(0,0,36.15) rot=(0,0,1;0rad)
  Solid = false
  Source = -> Face014
  Symmetric = false
FEATURE [Part::MultiFuse] Fusion015  label="plugHousing024"
  Placement = pos=(0,0,0) rot=(0,0,1;1.5708rad)
  Shapes = -> [Revolve010,Revolve015]
FEATURE [Part::Revolution] Revolve014  label="plugHousing026"
  Angle = 360
  Axis = (0,1,0)
  Base = (0,0,0)
  FaceMakerClass = Part::FaceMakerBullseye
  Placement = pos=(0,0,36.15) rot=(0,0,1;0rad)
  Solid = false
  Source = -> Face011
  Symmetric = false
FEATURE [Part::Revolution] Revolve013  label="plugHousing025"
  Angle = 360
  Axis = (0,1,0)
  Base = (0,0,0)
  FaceMakerClass = Part::FaceMakerBullseye
  Placement = pos=(0,0,36.15) rot=(0,0,1;0rad)
  Solid = false
  Source = -> Face015
  Symmetric = false
FEATURE [Part::MultiFuse] Fusion016  label="plugHousing028"
  Placement = pos=(0,19,0) rot=(0,0,1;3.14159rad)
  Shapes = -> [Fusion014,Fusion013]
FEATURE [Part::MultiFuse] Fusion011  label="plugHousing018"
  Placement = pos=(0,0,0) rot=(0,0,1;1.5708rad)
  Shapes = -> [Revolve014,Revolve013]
FEATURE [Part::MultiFuse] Fusion012  label="plugHousing019"
  Placement = pos=(0,19,0) rot=(0,0,1;3.14159rad)
  Shapes = -> [Fusion011,Fusion015]
FEATURE [Part::MultiFuse] Fusion017  label="plugHousing029"
  Placement = pos=(122.621,0,-0.15) rot=(0,0,1;0rad)
  Shapes = -> [Fusion016,Fusion012]
FEATURE [Part::MultiFuse] Fusion052  label="casePillarRetainers"
  Shapes = -> [Extrude012,Extrude013,Extrude014,Extrude015,Extrude016,Extrude017,Extrude018,Extrude019,Box011,Box012]
FEATURE [Part::Feature] Face077
  shape: bbox 3.5 x 17.8 x 2e-07 mm, 1 faces, 0 solids (baked)
FEATURE [Part::Revolution] Revolve081  label="removeToCreateScrewAndThreadedInsertHole018"
  Angle = 360
  Axis = (0,1,0)
  Base = (0,0,0)
  FaceMakerClass = Part::FaceMakerBullseye
  Placement = pos=(62.3,30.3,19.7) rot=(0,0,1;0rad)
  Solid = false
  Source = -> Face077
  Symmetric = false
FEATURE [Part::Feature] Face078
  shape: bbox 3.5 x 17.8 x 2e-07 mm, 1 faces, 0 solids (baked)
FEATURE [Part::Revolution] Revolve082  label="removeToCreateScrewAndThreadedInsertHole019"
  Angle = 360
  Axis = (0,1,0)
  Base = (0,0,0)
  FaceMakerClass = Part::FaceMakerBullseye
  Placement = pos=(62.3,30.3,51.7) rot=(0,0,1;0rad)
  Solid = false
  Source = -> Face078
  Symmetric = false
FEATURE [Part::Feature] Face079
  shape: bbox 3.5 x 17.8 x 2e-07 mm, 1 faces, 0 solids (baked)
FEATURE [Part::Revolution] Revolve083  label="removeToCreateScrewAndThreadedInsertHole020"
  Angle = 360
  Axis = (0,1,0)
  Base = (0,0,0)
  FaceMakerClass = Part::FaceMakerBullseye
  Placement = pos=(30.3,30.3,19.7) rot=(0,0,1;0rad)
  Solid = false
  Source = -> Face079
  Symmetric = false
FEATURE [Part::Feature] Face080
  shape: bbox 3.5 x 17.8 x 2e-07 mm, 1 faces, 0 solids (baked)
FEATURE [Part::Revolution] Revolve084  label="removeToCreateScrewAndThreadedInsertHole021"
  Angle = 360
  Axis = (0,1,0)
  Base = (0,0,0)
  FaceMakerClass = Part::FaceMakerBullseye
  Placement = pos=(30.3,30.3,51.7) rot=(0,0,1;0rad)
  Solid = false
  Source = -> Face080
  Symmetric = false
FEATURE [Part::MultiFuse] Fusion053  label="createThreadedInsertHolesForFan"
  Shapes = -> [Revolve081,Revolve082,Revolve083,Revolve084]
FEATURE [Part::Cut] Cut017  label="fanScrewHousing001"
  Base = -> Fusion046
  Tool = -> Fusion053
FEATURE [Part::Feature] Face081
  shape: bbox 3.5 x 17.8 x 2e-07 mm, 1 faces, 0 solids (baked)
FEATURE [Part::Revolution] Revolve085  label="removeToCreateScrewAndThreadedInsertHole022"
  Angle = 360
  Axis = (0,1,0)
  Base = (0,0,0)
  FaceMakerClass = Part::FaceMakerBullseye
  Placement = pos=(62.3,30.3,19.7) rot=(0,0,1;0rad)
  Solid = false
  Source = -> Face081
  Symmetric = false
FEATURE [Part::Feature] Face082
  shape: bbox 3.5 x 17.8 x 2e-07 mm, 1 faces, 0 solids (baked)
FEATURE [Part::Revolution] Revolve086  label="removeToCreateScrewAndThreadedInsertHole023"
  Angle = 360
  Axis = (0,1,0)
  Base = (0,0,0)
  FaceMakerClass = Part::FaceMakerBullseye
  Placement = pos=(62.3,30.3,51.7) rot=(0,0,1;0rad)
  Solid = false
  Source = -> Face082
  Symmetric = false
FEATURE [Part::Feature] Face083
  shape: bbox 3.5 x 17.8 x 2e-07 mm, 1 faces, 0 solids (baked)
FEATURE [Part::Revolution] Revolve087  label="removeToCreateScrewAndThreadedInsertHole024"
  Angle = 360
  Axis = (0,1,0)
  Base = (0,0,0)
  FaceMakerClass = Part::FaceMakerBullseye
  Placement = pos=(30.3,30.3,19.7) rot=(0,0,1;0rad)
  Solid = false
  Source = -> Face083
  Symmetric = false
FEATURE [Part::Feature] Face084
  shape: bbox 3.5 x 17.8 x 2e-07 mm, 1 faces, 0 solids (baked)
FEATURE [Part::Revolution] Revolve088  label="removeToCreateScrewAndThreadedInsertHole025"
  Angle = 360
  Axis = (0,1,0)
  Base = (0,0,0)
  FaceMakerClass = Part::FaceMakerBullseye
  Placement = pos=(30.3,30.3,51.7) rot=(0,0,1;0rad)
  Solid = false
  Source = -> Face084
  Symmetric = false
FEATURE [Part::MultiFuse] Fusion054  label="createThreadedInsertHolesForFan001"
  Shapes = -> [Revolve085,Revolve086,Revolve087,Revolve088]
FEATURE [Part::Cut] Cut018  label="top007"
  Base = -> Fusion040
  Tool = -> Fusion054
FEATURE [Sketcher::SketchObject] Sketch029
  FullyConstrained = false
  Placement = pos=(0,0,0) rot=(1,0,0;1.5708rad)
  sketch-geometry (24):
    g0: ArcOfCircle CenterX=-4 CenterY=-10.5 CenterZ=0 NormalX=0 NormalY=0 NormalZ=1 AngleXU=0 Radius=1.5 StartAngle=6e-16 EndAngle=3.14159
    g1: ArcOfCircle CenterX=-34.2 CenterY=-10.5 CenterZ=0 NormalX=0 NormalY=0 NormalZ=1 AngleXU=0 Radius=1.5 StartAngle=0 EndAngle=3.14159
    g2: ArcOfCircle CenterX=-34.2 CenterY=-27.7 CenterZ=0 NormalX=0 NormalY=0 NormalZ=1 AngleXU=0 Radius=1.5 StartAngle=3.14159 EndAngle=6.28319
    g3: ArcOfCircle CenterX=-4 CenterY=-27.7 CenterZ=0 NormalX=0 NormalY=0 NormalZ=1 AngleXU=0 Radius=1.5 StartAngle=3.1416 EndAngle=6.28319
    g4: ArcOfCircle CenterX=-10 CenterY=-4.3 CenterZ=0 NormalX=0 NormalY=0 NormalZ=1 AngleXU=0 Radius=1.5 StartAngle=2e-16 EndAngle=3.14159
    g5: ArcOfCircle CenterX=-16.1 CenterY=-1.8 CenterZ=0 NormalX=0 NormalY=0 NormalZ=1 AngleXU=0 Radius=1.5 StartAngle=5e-16 EndAngle=3.14159
    g6: ArcOfCircle CenterX=-22.1 CenterY=-1.8 CenterZ=0 NormalX=0 NormalY=0 NormalZ=1 AngleXU=0 Radius=1.5 StartAngle=5e-16 EndAngle=3.14159
    g7: ArcOfCircle CenterX=-28.2 CenterY=-4.3 CenterZ=0 NormalX=0 NormalY=0 NormalZ=1 AngleXU=0 Radius=1.5 StartAngle=2e-16 EndAngle=3.14159
    g8: ArcOfCircle CenterX=-10 CenterY=-33.9 CenterZ=0 NormalX=0 NormalY=0 NormalZ=1 AngleXU=0 Radius=1.5 StartAngle=3.14159 EndAngle=6.28319
    g9: ArcOfCircle CenterX=-16.1 CenterY=-36.4 CenterZ=0 NormalX=0 NormalY=0 NormalZ=1 AngleXU=0 Radius=1.5 StartAngle=3.14159 EndAngle=6.28319
    g10: ArcOfCircle CenterX=-22.1 CenterY=-36.4 CenterZ=0 NormalX=0 NormalY=0 NormalZ=1 AngleXU=0 Radius=1.5 StartAngle=3.14159 EndAngle=6.28319
    g11: ArcOfCircle CenterX=-28.2 CenterY=-33.9 CenterZ=0 NormalX=0 NormalY=0 NormalZ=1 AngleXU=0 Radius=1.5 StartAngle=3.14159 EndAngle=6.28319
    g12: LineSegment StartX=-35.7 StartY=-10.5 StartZ=0 EndX=-35.7 EndY=-27.7 EndZ=0
    g13: LineSegment StartX=-32.7 StartY=-10.5 StartZ=0 EndX=-32.7 EndY=-27.7 EndZ=0
    g14: LineSegment StartX=-29.7 StartY=-33.9 StartZ=0 EndX=-29.7 EndY=-4.3 EndZ=0
    g15: LineSegment StartX=-26.7 StartY=-33.9 StartZ=0 EndX=-26.7 EndY=-4.3 EndZ=0
    g16: LineSegment StartX=-2.5 StartY=-10.5 StartZ=0 EndX=-2.5 EndY=-27.7 EndZ=0
    g17: LineSegment StartX=-8.5 StartY=-4.3 StartZ=0 EndX=-8.5 EndY=-33.9 EndZ=0
    g18: LineSegment StartX=-5.5 StartY=-10.5 StartZ=0 EndX=-5.5 EndY=-27.7 EndZ=0
    g19: LineSegment StartX=-11.5 StartY=-4.3 StartZ=0 EndX=-11.5 EndY=-33.9 EndZ=0
    g20: LineSegment StartX=-14.6 StartY=-1.8 StartZ=0 EndX=-14.6 EndY=-36.4 EndZ=0
    g21: LineSegment StartX=-17.6 StartY=-1.8 StartZ=0 EndX=-17.6 EndY=-36.4 EndZ=0
    g22: LineSegment StartX=-20.6 StartY=-36.4 StartZ=0 EndX=-20.6 EndY=-1.8 EndZ=0
    g23: LineSegment StartX=-23.6 StartY=-1.8 StartZ=0 EndX=-23.6 EndY=-36.4 EndZ=0
  constraints (48):
    c: Block(g0)
    c: Block(g1)
    c: Block(g2)
    c: Block(g3)
    c: Block(g4)
    c: Block(g5)
    c: Block(g6)
    c: Block(g7)
    c: Block(g8)
    c: Block(g9)
    c: Block(g10)
    c: Block(g11)
    c: Coincident(g12,g1)
    c: Coincident(g12,g2)
    c: Vertical(g12)
    c: Coincident(g13,g1)
    c: Coincident(g13,g2)
    c: Vertical(g13)
    c: Coincident(g14,g11)
    c: Coincident(g14,g7)
    c: Vertical(g14)
    c: Coincident(g15,g11)
    c: Coincident(g15,g7)
    c: Vertical(g15)
    c: Coincident(g16,g0)
    c: Coincident(g16,g3)
    c: Vertical(g16)
    c: Coincident(g17,g4)
    c: Coincident(g17,g8)
    c: Vertical(g17)
    c: Coincident(g18,g0)
    c: Coincident(g18,g3)
    c: Vertical(g18)
    c: Coincident(g19,g4)
    c: Coincident(g19,g8)
    c: Vertical(g19)
    c: Coincident(g20,g5)
    c: Coincident(g20,g9)
    c: Vertical(g20)
    c: Coincident(g21,g5)
    c: Coincident(g21,g9)
    c: Vertical(g21)
    c: Coincident(g22,g10)
    c: Coincident(g22,g6)
    c: Vertical(g22)
    c: Coincident(g23,g6)
    c: Coincident(g23,g10)
    c: Vertical(g23)
FEATURE [Part::Extrusion] Extrude020  label="removeToCreateFanGrillHoles"
  Base = -> Sketch029
  Dir = (0,-1,6e-16)
  DirMode = 2
  FaceMakerClass = Part::FaceMakerBullseye
  LengthFwd = 10
  LengthRev = 0
  Placement = pos=(65.4,44,54.82) rot=(0,0,1;0rad)
  Solid = true
  Symmetric = false
FEATURE [Part::MultiFuse] Fusion055  label="top008"
  Shapes = -> [Cut017,Cut018]
FEATURE [Part::Cut] Cut019  label="top009"
  Base = -> Fusion055
  Tool = -> Extrude020
FEATURE [App::MeasureDistance] Distance003  label="Distance: 71.95 mm"
  Distance = 71.9513
  P1 = (117,38,72)
  P2 = (117,38,0.0487319)
FEATURE [Sketcher::SketchObject] Sketch030
  FullyConstrained = true
  Placement = pos=(117,19,0) rot=(0.57735,0.57735,0.57735;2.0944rad)
  sketch-geometry (48):
    g0: LineSegment StartX=-49.19 StartY=69.25 StartZ=0 EndX=-49.19 EndY=66.25 EndZ=0
    g1: LineSegment StartX=-49.19 StartY=63.5 StartZ=0 EndX=-49.19 EndY=60.5 EndZ=0
    g2: LineSegment StartX=-49.19 StartY=57.75 StartZ=0 EndX=-49.19 EndY=54.75 EndZ=0
    g3: LineSegment StartX=-49.19 StartY=52 StartZ=0 EndX=-49.19 EndY=49 EndZ=0
    g4: LineSegment StartX=-49.19 StartY=46.25 StartZ=0 EndX=-49.19 EndY=43.25 EndZ=0
    g5: LineSegment StartX=-49.19 StartY=40.5 StartZ=0 EndX=-49.19 EndY=37.5 EndZ=0
    g6: LineSegment StartX=-49.19 StartY=34.5 StartZ=0 EndX=-49.19 EndY=31.5 EndZ=0
    g7: LineSegment StartX=-49.19 StartY=28.75 StartZ=0 EndX=-49.19 EndY=25.75 EndZ=0
    g8: LineSegment StartX=-49.19 StartY=23 StartZ=0 EndX=-49.19 EndY=20 EndZ=0
    g9: LineSegment StartX=-49.19 StartY=17.25 StartZ=0 EndX=-49.19 EndY=14.25 EndZ=0
    g10: LineSegment StartX=-49.19 StartY=11.5 StartZ=0 EndX=-49.19 EndY=8.5 EndZ=0
    g11: LineSegment StartX=-49.19 StartY=5.75 StartZ=0 EndX=-49.19 EndY=2.75 EndZ=0
    g12: ArcOfCircle CenterX=-1.5 CenterY=67.75 CenterZ=0 NormalX=0 NormalY=0 NormalZ=1 AngleXU=0 Radius=1.5 StartAngle=4.71239 EndAngle=7.85398
    g13: ArcOfCircle CenterX=-1.5 CenterY=62 CenterZ=0 NormalX=0 NormalY=0 NormalZ=1 AngleXU=0 Radius=1.5 StartAngle=4.71239 EndAngle=7.85398
    g14: ArcOfCircle CenterX=-1.5 CenterY=56.25 CenterZ=0 NormalX=0 NormalY=0 NormalZ=1 AngleXU=0 Radius=1.5 StartAngle=4.71239 EndAngle=7.85398
    g15: ArcOfCircle CenterX=-11.49 CenterY=50.5 CenterZ=0 NormalX=0 NormalY=0 NormalZ=1 AngleXU=0 Radius=1.5 StartAngle=4.71239 EndAngle=7.85398
    g16: ArcOfCircle CenterX=-16.28 CenterY=44.75 CenterZ=0 NormalX=0 NormalY=0 NormalZ=1 AngleXU=0 Radius=1.5 StartAngle=4.71239 EndAngle=7.85398
    g17: ArcOfCircle CenterX=-18.2337 CenterY=39 CenterZ=0 NormalX=0 NormalY=0 NormalZ=1 AngleXU=0 Radius=1.5 StartAngle=4.71485 EndAngle=7.85398
    g18: ArcOfCircle CenterX=-16.2837 CenterY=27.25 CenterZ=0 NormalX=0 NormalY=0 NormalZ=1 AngleXU=0 Radius=1.5 StartAngle=4.71485 EndAngle=7.85398
    g19: ArcOfCircle CenterX=-18.2337 CenterY=33 CenterZ=0 NormalX=0 NormalY=0 NormalZ=1 AngleXU=0 Radius=1.5 StartAngle=4.71485 EndAngle=7.85398
    g20: ArcOfCircle CenterX=-11.49 CenterY=21.5 CenterZ=0 NormalX=0 NormalY=0 NormalZ=1 AngleXU=0 Radius=1.5 StartAngle=4.71239 EndAngle=7.85398
    g21: ArcOfCircle CenterX=-1.5 CenterY=4.25 CenterZ=0 NormalX=0 NormalY=0 NormalZ=1 AngleXU=0 Radius=1.5 StartAngle=4.71239 EndAngle=7.85398
    g22: ArcOfCircle CenterX=-1.5 CenterY=10 CenterZ=0 NormalX=0 NormalY=0 NormalZ=1 AngleXU=0 Radius=1.5 StartAngle=4.71239 EndAngle=7.85398
    g23: ArcOfCircle CenterX=-1.5 CenterY=15.75 CenterZ=0 NormalX=0 NormalY=0 NormalZ=1 AngleXU=0 Radius=1.5 StartAngle=4.71239 EndAngle=7.85398
    g24: LineSegment StartX=-49.19 StartY=69.25 StartZ=0 EndX=-1.5 EndY=69.25 EndZ=0
    g25: LineSegment StartX=-49.19 StartY=66.25 StartZ=0 EndX=-1.5 EndY=66.25 EndZ=0
    g26: LineSegment StartX=-49.19 StartY=63.5 StartZ=0 EndX=-1.5 EndY=63.5 EndZ=0
    g27: LineSegment StartX=-49.19 StartY=60.5 StartZ=0 EndX=-1.5 EndY=60.5 EndZ=0
    g28: LineSegment StartX=-49.19 StartY=57.75 StartZ=0 EndX=-1.5 EndY=57.75 EndZ=0
    g29: LineSegment StartX=-49.19 StartY=54.75 StartZ=0 EndX=-1.5 EndY=54.75 EndZ=0
    g30: LineSegment StartX=-49.19 StartY=52 StartZ=0 EndX=-11.49 EndY=52 EndZ=0
    g31: LineSegment StartX=-49.19 StartY=49 StartZ=0 EndX=-11.49 EndY=49 EndZ=0
    g32: LineSegment StartX=-49.19 StartY=46.25 StartZ=0 EndX=-16.28 EndY=46.25 EndZ=0
    g33: LineSegment StartX=-49.19 StartY=43.25 StartZ=0 EndX=-16.28 EndY=43.25 EndZ=0
    g34: LineSegment StartX=-49.19 StartY=40.5 StartZ=0 EndX=-18.2337 EndY=40.5 EndZ=0
    g35: LineSegment StartX=-49.19 StartY=37.5 StartZ=0 EndX=-18.23 EndY=37.5 EndZ=0
    g36: LineSegment StartX=-49.19 StartY=34.5 StartZ=0 EndX=-18.2337 EndY=34.5 EndZ=0
    g37: LineSegment StartX=-49.19 StartY=31.5 StartZ=0 EndX=-18.23 EndY=31.5 EndZ=0
    g38: LineSegment StartX=-49.19 StartY=28.75 StartZ=0 EndX=-16.2837 EndY=28.75 EndZ=0
    g39: LineSegment StartX=-49.19 StartY=25.75 StartZ=0 EndX=-16.28 EndY=25.75 EndZ=0
    g40: LineSegment StartX=-49.19 StartY=23 StartZ=0 EndX=-11.49 EndY=23 EndZ=0
    g41: LineSegment StartX=-49.19 StartY=20 StartZ=0 EndX=-11.49 EndY=20 EndZ=0
    g42: LineSegment StartX=-49.19 StartY=17.25 StartZ=0 EndX=-1.5 EndY=17.25 EndZ=0
    g43: LineSegment StartX=-49.19 StartY=14.25 StartZ=0 EndX=-1.5 EndY=14.25 EndZ=0
    g44: LineSegment StartX=-49.19 StartY=11.5 StartZ=0 EndX=-1.5 EndY=11.5 EndZ=0
    g45: LineSegment StartX=-49.19 StartY=8.5 StartZ=0 EndX=-1.5 EndY=8.5 EndZ=0
    g46: LineSegment StartX=-49.19 StartY=5.75 StartZ=0 EndX=-1.5 EndY=5.75 EndZ=0
    g47: LineSegment StartX=-49.19 StartY=2.75 StartZ=0 EndX=-1.5 EndY=2.75 EndZ=0
  constraints (120):
    c: Vertical(g0)
    c: Distance(g0) = 3
    c: Block(g0)
    c: Vertical(g1)
    c: Distance(g1) = 3
    c: Vertical(g2)
    c: Equal(g0,g2) = 3
    c: Block(g2)
    c: Vertical(g3)
    c: Equal(g1,g3) = 3
    c: Vertical(g4)
    c: Equal(g0,g4) = 3
    c: Block(g4)
    c: Vertical(g5)
    c: Equal(g1,g5) = 3
    c: Vertical(g6)
    c: Equal(g0,g6) = 3
    c: Block(g6)
    c: Vertical(g7)
    c: Equal(g1,g7) = 3
    c: Vertical(g8)
    c: Equal(g0,g8) = 3
    c: Block(g8)
    c: Vertical(g9)
    c: Equal(g1,g9) = 3
    c: Vertical(g10)
    c: Equal(g0,g10) = 3
    c: Block(g10)
    c: Vertical(g11)
    c: Equal(g1,g11) = 3
    c: Block(g12)
    c: Block(g13)
    c: Block(g14)
    c: Block(g15)
    c: Block(g16)
    c: Block(g17)
    c: Block(g18)
    c: Block(g19)
    c: Block(g20)
    c: Block(g21)
    c: Block(g22)
    c: Block(g23)
    c: Block(g11)
    c: Block(g9)
    c: Block(g7)
    c: Block(g5)
    c: Block(g3)
    c: Block(g1)
    c: Coincident(g24,g0)
    c: Coincident(g24,g12)
    c: Horizontal(g24)
    c: Coincident(g25,g0)
    c: Coincident(g25,g12)
    c: Horizontal(g25)
    c: Coincident(g26,g1)
    c: Coincident(g26,g13)
    c: Horizontal(g26)
    c: Coincident(g27,g1)
    c: Coincident(g27,g13)
    c: Horizontal(g27)
    c: Coincident(g28,g2)
    c: Coincident(g28,g14)
    c: Horizontal(g28)
    c: Coincident(g29,g2)
    c: Coincident(g29,g14)
    c: Horizontal(g29)
    c: Coincident(g30,g3)
    c: Coincident(g30,g15)
    c: Horizontal(g30)
    c: Coincident(g31,g3)
    c: Coincident(g31,g15)
    c: Horizontal(g31)
    c: Coincident(g32,g4)
    c: Coincident(g32,g16)
    c: Horizontal(g32)
    c: Coincident(g33,g4)
    c: Coincident(g33,g16)
    c: Horizontal(g33)
    c: Coincident(g34,g5)
    c: Coincident(g34,g17)
    c: Horizontal(g34)
    c: Coincident(g35,g5)
    c: Coincident(g35,g17)
    c: Horizontal(g35)
    c: Coincident(g36,g6)
    c: Coincident(g36,g19)
    c: Horizontal(g36)
    c: Coincident(g37,g6)
    c: Coincident(g37,g19)
    c: Horizontal(g37)
    c: Coincident(g38,g7)
    c: Coincident(g38,g18)
    c: Horizontal(g38)
    c: Coincident(g39,g7)
    c: Coincident(g39,g18)
    c: Horizontal(g39)
    c: Coincident(g40,g8)
    c: Coincident(g40,g20)
    c: Horizontal(g40)
    c: Coincident(g41,g8)
    c: Coincident(g41,g20)
    c: Horizontal(g41)
    c: Coincident(g42,g9)
    c: Coincident(g42,g23)
    c: Horizontal(g42)
    c: Coincident(g43,g9)
    c: Coincident(g43,g23)
    c: Horizontal(g43)
    c: Coincident(g44,g10)
    c: Coincident(g44,g22)
    c: Horizontal(g44)
    c: Coincident(g45,g10)
    c: Coincident(g45,g22)
    c: Horizontal(g45)
    c: Coincident(g46,g11)
    c: Coincident(g46,g21)
    c: Horizontal(g46)
    c: Coincident(g47,g11)
    c: Coincident(g47,g21)
    c: Horizontal(g47)
FEATURE [Sketcher::SketchObject] Sketch031
  FullyConstrained = true
  Placement = pos=(117,19,0) rot=(0.57735,0.57735,0.57735;2.0944rad)
  sketch-geometry (24):
    g0: ArcOfCircle CenterX=-49.19 CenterY=67.75 CenterZ=0 NormalX=0 NormalY=0 NormalZ=1 AngleXU=0 Radius=1.5 StartAngle=1.5708 EndAngle=4.71239
    g1: ArcOfCircle CenterX=-49.19 CenterY=62 CenterZ=0 NormalX=0 NormalY=0 NormalZ=1 AngleXU=0 Radius=1.5 StartAngle=1.5708 EndAngle=4.71239
    g2: ArcOfCircle CenterX=-49.19 CenterY=56.25 CenterZ=0 NormalX=0 NormalY=0 NormalZ=1 AngleXU=0 Radius=1.5 StartAngle=1.5708 EndAngle=4.71239
    g3: ArcOfCircle CenterX=-49.19 CenterY=50.5 CenterZ=0 NormalX=0 NormalY=0 NormalZ=1 AngleXU=0 Radius=1.5 StartAngle=1.5708 EndAngle=4.71239
    g4: ArcOfCircle CenterX=-49.19 CenterY=44.75 CenterZ=0 NormalX=0 NormalY=0 NormalZ=1 AngleXU=0 Radius=1.5 StartAngle=1.5708 EndAngle=4.71239
    g5: ArcOfCircle CenterX=-49.19 CenterY=39 CenterZ=0 NormalX=0 NormalY=0 NormalZ=1 AngleXU=0 Radius=1.5 StartAngle=1.5708 EndAngle=4.71239
    g6: ArcOfCircle CenterX=-49.19 CenterY=33 CenterZ=0 NormalX=0 NormalY=0 NormalZ=1 AngleXU=0 Radius=1.5 StartAngle=1.5708 EndAngle=4.71239
    g7: ArcOfCircle CenterX=-49.19 CenterY=27.25 CenterZ=0 NormalX=0 NormalY=0 NormalZ=1 AngleXU=0 Radius=1.5 StartAngle=1.5708 EndAngle=4.71239
    g8: ArcOfCircle CenterX=-49.19 CenterY=21.5 CenterZ=0 NormalX=0 NormalY=0 NormalZ=1 AngleXU=0 Radius=1.5 StartAngle=1.5708 EndAngle=4.71239
    g9: ArcOfCircle CenterX=-49.19 CenterY=15.75 CenterZ=0 NormalX=0 NormalY=0 NormalZ=1 AngleXU=0 Radius=1.5 StartAngle=1.5708 EndAngle=4.71239
    g10: ArcOfCircle CenterX=-49.19 CenterY=10 CenterZ=0 NormalX=0 NormalY=0 NormalZ=1 AngleXU=0 Radius=1.5 StartAngle=1.5708 EndAngle=4.71239
    g11: ArcOfCircle CenterX=-49.19 CenterY=4.25 CenterZ=0 NormalX=0 NormalY=0 NormalZ=1 AngleXU=0 Radius=1.5 StartAngle=1.5708 EndAngle=4.71239
    g12: LineSegment StartX=-49.19 StartY=69.25 StartZ=0 EndX=-49.19 EndY=66.25 EndZ=0
    g13: LineSegment StartX=-49.19 StartY=63.5 StartZ=0 EndX=-49.19 EndY=60.5 EndZ=0
    g14: LineSegment StartX=-49.19 StartY=57.75 StartZ=0 EndX=-49.19 EndY=54.75 EndZ=0
    g15: LineSegment StartX=-49.19 StartY=52 StartZ=0 EndX=-49.19 EndY=49 EndZ=0
    g16: LineSegment StartX=-49.19 StartY=46.25 StartZ=0 EndX=-49.19 EndY=43.25 EndZ=0
    g17: LineSegment StartX=-49.19 StartY=40.5 StartZ=0 EndX=-49.19 EndY=37.5 EndZ=0
    g18: LineSegment StartX=-49.19 StartY=34.5 StartZ=0 EndX=-49.19 EndY=31.5 EndZ=0
    g19: LineSegment StartX=-49.19 StartY=28.75 StartZ=0 EndX=-49.19 EndY=25.75 EndZ=0
    g20: LineSegment StartX=-49.19 StartY=23 StartZ=0 EndX=-49.19 EndY=20 EndZ=0
    g21: LineSegment StartX=-49.19 StartY=17.25 StartZ=0 EndX=-49.19 EndY=14.25 EndZ=0
    g22: LineSegment StartX=-49.19 StartY=11.5 StartZ=0 EndX=-49.19 EndY=8.5 EndZ=0
    g23: LineSegment StartX=-49.19 StartY=5.75 StartZ=0 EndX=-49.19 EndY=2.75 EndZ=0
  constraints (48):
    c: Block(g0)
    c: Block(g1)
    c: Block(g2)
    c: Block(g3)
    c: Block(g4)
    c: Block(g5)
    c: Block(g6)
    c: Block(g7)
    c: Block(g8)
    c: Block(g9)
    c: Block(g10)
    c: Block(g11)
    c: Coincident(g12,g0)
    c: Coincident(g12,g0)
    c: Vertical(g12)
    c: Vertical(g13)
    c: Coincident(g13,g1)
    c: Vertical(g14)
    c: Coincident(g14,g2)
    c: Vertical(g15)
    c: Coincident(g15,g3)
    c: Vertical(g16)
    c: Coincident(g16,g4)
    c: Vertical(g17)
    c: Coincident(g17,g5)
    c: Vertical(g18)
    c: Coincident(g18,g6)
    c: Vertical(g19)
    c: Coincident(g19,g7)
    c: Vertical(g20)
    c: Coincident(g20,g8)
    c: Vertical(g21)
    c: Coincident(g21,g9)
    c: Vertical(g22)
    c: Coincident(g22,g10)
    c: Vertical(g23)
    c: Coincident(g23,g11)
    c: Block(g23)
    c: Block(g22)
    c: Block(g21)
    c: Block(g20)
    c: Block(g13)
    c: Block(g14)
    c: Block(g15)
    c: Block(g16)
    c: Block(g17)
    c: Block(g18)
    c: Block(g19)
FEATURE [Part::Extrusion] Extrude022
  Base = -> Sketch030
  Dir = (1,-2e-16,2e-16)
  DirMode = 2
  FaceMakerClass = Part::FaceMakerBullseye
  LengthFwd = 19
  LengthRev = 0
  Placement = pos=(-19,0,0) rot=(0,0,1;0rad)
  Solid = true
  Symmetric = false
FEATURE [Part::Fillet] Fillet022
  Base = -> Extrude022
  Edges = 24 edges r=1.49: [Edge6,Edge11,Edge18,Edge23,Edge30,Edge35,Edge42,Edge47,Edge54,Edge59,Edge66,Edge71,Edge78,Edge83,Edge90,Edge95,Edge102,Edge107,Edge114,Edge119,Edge126,Edge131,Edge138,Edge143]
FEATURE [Part::Cut] Cut020  label="top010"
  Base = -> Cut019
  Tool = -> Fillet022
FEATURE [Sketcher::SketchObject] Sketch032
  FullyConstrained = true
  Placement = pos=(117,19,0) rot=(0.57735,0.57735,0.57735;2.0944rad)
  sketch-geometry (48):
    g0: LineSegment StartX=-49.19 StartY=69.25 StartZ=0 EndX=-49.19 EndY=66.25 EndZ=0
    g1: LineSegment StartX=-49.19 StartY=63.5 StartZ=0 EndX=-49.19 EndY=60.5 EndZ=0
    g2: LineSegment StartX=-49.19 StartY=57.75 StartZ=0 EndX=-49.19 EndY=54.75 EndZ=0
    g3: LineSegment StartX=-49.19 StartY=52 StartZ=0 EndX=-49.19 EndY=49 EndZ=0
    g4: LineSegment StartX=-49.19 StartY=46.25 StartZ=0 EndX=-49.19 EndY=43.25 EndZ=0
    g5: LineSegment StartX=-49.19 StartY=40.5 StartZ=0 EndX=-49.19 EndY=37.5 EndZ=0
    g6: LineSegment StartX=-49.19 StartY=34.5 StartZ=0 EndX=-49.19 EndY=31.5 EndZ=0
    g7: LineSegment StartX=-49.19 StartY=28.75 StartZ=0 EndX=-49.19 EndY=25.75 EndZ=0
    g8: LineSegment StartX=-49.19 StartY=23 StartZ=0 EndX=-49.19 EndY=20 EndZ=0
    g9: LineSegment StartX=-49.19 StartY=17.25 StartZ=0 EndX=-49.19 EndY=14.25 EndZ=0
    g10: LineSegment StartX=-49.19 StartY=11.5 StartZ=0 EndX=-49.19 EndY=8.5 EndZ=0
    g11: LineSegment StartX=-49.19 StartY=5.75 StartZ=0 EndX=-49.19 EndY=2.75 EndZ=0
    g12: ArcOfCircle CenterX=-1.5 CenterY=67.75 CenterZ=0 NormalX=0 NormalY=0 NormalZ=1 AngleXU=0 Radius=1.5 StartAngle=4.71239 EndAngle=7.85398
    g13: ArcOfCircle CenterX=-1.5 CenterY=62 CenterZ=0 NormalX=0 NormalY=0 NormalZ=1 AngleXU=0 Radius=1.5 StartAngle=4.71239 EndAngle=7.85398
    g14: ArcOfCircle CenterX=-1.5 CenterY=56.25 CenterZ=0 NormalX=0 NormalY=0 NormalZ=1 AngleXU=0 Radius=1.5 StartAngle=4.71239 EndAngle=7.85398
    g15: ArcOfCircle CenterX=-11.49 CenterY=50.5 CenterZ=0 NormalX=0 NormalY=0 NormalZ=1 AngleXU=0 Radius=1.5 StartAngle=4.71239 EndAngle=7.85398
    g16: ArcOfCircle CenterX=-16.28 CenterY=44.75 CenterZ=0 NormalX=0 NormalY=0 NormalZ=1 AngleXU=0 Radius=1.5 StartAngle=4.71239 EndAngle=7.85398
    g17: ArcOfCircle CenterX=-18.2337 CenterY=39 CenterZ=0 NormalX=0 NormalY=0 NormalZ=1 AngleXU=0 Radius=1.5 StartAngle=4.71485 EndAngle=7.85398
    g18: ArcOfCircle CenterX=-16.2837 CenterY=27.25 CenterZ=0 NormalX=0 NormalY=0 NormalZ=1 AngleXU=0 Radius=1.5 StartAngle=4.71485 EndAngle=7.85398
    g19: ArcOfCircle CenterX=-18.2337 CenterY=33 CenterZ=0 NormalX=0 NormalY=0 NormalZ=1 AngleXU=0 Radius=1.5 StartAngle=4.71485 EndAngle=7.85398
    g20: ArcOfCircle CenterX=-11.49 CenterY=21.5 CenterZ=0 NormalX=0 NormalY=0 NormalZ=1 AngleXU=0 Radius=1.5 StartAngle=4.71239 EndAngle=7.85398
    g21: ArcOfCircle CenterX=-1.5 CenterY=4.25 CenterZ=0 NormalX=0 NormalY=0 NormalZ=1 AngleXU=0 Radius=1.5 StartAngle=4.71239 EndAngle=7.85398
    g22: ArcOfCircle CenterX=-1.5 CenterY=10 CenterZ=0 NormalX=0 NormalY=0 NormalZ=1 AngleXU=0 Radius=1.5 StartAngle=4.71239 EndAngle=7.85398
    g23: ArcOfCircle CenterX=-1.5 CenterY=15.75 CenterZ=0 NormalX=0 NormalY=0 NormalZ=1 AngleXU=0 Radius=1.5 StartAngle=4.71239 EndAngle=7.85398
    g24: LineSegment StartX=-49.19 StartY=69.25 StartZ=0 EndX=-1.5 EndY=69.25 EndZ=0
    g25: LineSegment StartX=-49.19 StartY=66.25 StartZ=0 EndX=-1.5 EndY=66.25 EndZ=0
    g26: LineSegment StartX=-49.19 StartY=63.5 StartZ=0 EndX=-1.5 EndY=63.5 EndZ=0
    g27: LineSegment StartX=-49.19 StartY=60.5 StartZ=0 EndX=-1.5 EndY=60.5 EndZ=0
    g28: LineSegment StartX=-49.19 StartY=57.75 StartZ=0 EndX=-1.5 EndY=57.75 EndZ=0
    g29: LineSegment StartX=-49.19 StartY=54.75 StartZ=0 EndX=-1.5 EndY=54.75 EndZ=0
    g30: LineSegment StartX=-49.19 StartY=52 StartZ=0 EndX=-11.49 EndY=52 EndZ=0
    g31: LineSegment StartX=-49.19 StartY=49 StartZ=0 EndX=-11.49 EndY=49 EndZ=0
    g32: LineSegment StartX=-49.19 StartY=46.25 StartZ=0 EndX=-16.28 EndY=46.25 EndZ=0
    g33: LineSegment StartX=-49.19 StartY=43.25 StartZ=0 EndX=-16.28 EndY=43.25 EndZ=0
    g34: LineSegment StartX=-49.19 StartY=40.5 StartZ=0 EndX=-18.2337 EndY=40.5 EndZ=0
    g35: LineSegment StartX=-49.19 StartY=37.5 StartZ=0 EndX=-18.23 EndY=37.5 EndZ=0
    g36: LineSegment StartX=-49.19 StartY=34.5 StartZ=0 EndX=-18.2337 EndY=34.5 EndZ=0
    g37: LineSegment StartX=-49.19 StartY=31.5 StartZ=0 EndX=-18.23 EndY=31.5 EndZ=0
    g38: LineSegment StartX=-49.19 StartY=28.75 StartZ=0 EndX=-16.2837 EndY=28.75 EndZ=0
    g39: LineSegment StartX=-49.19 StartY=25.75 StartZ=0 EndX=-16.28 EndY=25.75 EndZ=0
    g40: LineSegment StartX=-49.19 StartY=23 StartZ=0 EndX=-11.49 EndY=23 EndZ=0
    g41: LineSegment StartX=-49.19 StartY=20 StartZ=0 EndX=-11.49 EndY=20 EndZ=0
    g42: LineSegment StartX=-49.19 StartY=17.25 StartZ=0 EndX=-1.5 EndY=17.25 EndZ=0
    g43: LineSegment StartX=-49.19 StartY=14.25 StartZ=0 EndX=-1.5 EndY=14.25 EndZ=0
    g44: LineSegment StartX=-49.19 StartY=11.5 StartZ=0 EndX=-1.5 EndY=11.5 EndZ=0
    g45: LineSegment StartX=-49.19 StartY=8.5 StartZ=0 EndX=-1.5 EndY=8.5 EndZ=0
    g46: LineSegment StartX=-49.19 StartY=5.75 StartZ=0 EndX=-1.5 EndY=5.75 EndZ=0
    g47: LineSegment StartX=-49.19 StartY=2.75 StartZ=0 EndX=-1.5 EndY=2.75 EndZ=0
  constraints (120):
    c: Vertical(g0)
    c: Distance(g0) = 3
    c: Block(g0)
    c: Vertical(g1)
    c: Distance(g1) = 3
    c: Vertical(g2)
    c: Equal(g0,g2) = 3
    c: Block(g2)
    c: Vertical(g3)
    c: Equal(g1,g3) = 3
    c: Vertical(g4)
    c: Equal(g0,g4) = 3
    c: Block(g4)
    c: Vertical(g5)
    c: Equal(g1,g5) = 3
    c: Vertical(g6)
    c: Equal(g0,g6) = 3
    c: Block(g6)
    c: Vertical(g7)
    c: Equal(g1,g7) = 3
    c: Vertical(g8)
    c: Equal(g0,g8) = 3
    c: Block(g8)
    c: Vertical(g9)
    c: Equal(g1,g9) = 3
    c: Vertical(g10)
    c: Equal(g0,g10) = 3
    c: Block(g10)
    c: Vertical(g11)
    c: Equal(g1,g11) = 3
    c: Block(g12)
    c: Block(g13)
    c: Block(g14)
    c: Block(g15)
    c: Block(g16)
    c: Block(g17)
    c: Block(g18)
    c: Block(g19)
    c: Block(g20)
    c: Block(g21)
    c: Block(g22)
    c: Block(g23)
    c: Block(g11)
    c: Block(g9)
    c: Block(g7)
    c: Block(g5)
    c: Block(g3)
    c: Block(g1)
    c: Coincident(g24,g0)
    c: Coincident(g24,g12)
    c: Horizontal(g24)
    c: Coincident(g25,g0)
    c: Coincident(g25,g12)
    c: Horizontal(g25)
    c: Coincident(g26,g1)
    c: Coincident(g26,g13)
    c: Horizontal(g26)
    c: Coincident(g27,g1)
    c: Coincident(g27,g13)
    c: Horizontal(g27)
    c: Coincident(g28,g2)
    c: Coincident(g28,g14)
    c: Horizontal(g28)
    c: Coincident(g29,g2)
    c: Coincident(g29,g14)
    c: Horizontal(g29)
    c: Coincident(g30,g3)
    c: Coincident(g30,g15)
    c: Horizontal(g30)
    c: Coincident(g31,g3)
    c: Coincident(g31,g15)
    c: Horizontal(g31)
    c: Coincident(g32,g4)
    c: Coincident(g32,g16)
    c: Horizontal(g32)
    c: Coincident(g33,g4)
    c: Coincident(g33,g16)
    c: Horizontal(g33)
    c: Coincident(g34,g5)
    c: Coincident(g34,g17)
    c: Horizontal(g34)
    c: Coincident(g35,g5)
    c: Coincident(g35,g17)
    c: Horizontal(g35)
    c: Coincident(g36,g6)
    c: Coincident(g36,g19)
    c: Horizontal(g36)
    c: Coincident(g37,g6)
    c: Coincident(g37,g19)
    c: Horizontal(g37)
    c: Coincident(g38,g7)
    c: Coincident(g38,g18)
    c: Horizontal(g38)
    c: Coincident(g39,g7)
    c: Coincident(g39,g18)
    c: Horizontal(g39)
    c: Coincident(g40,g8)
    c: Coincident(g40,g20)
    c: Horizontal(g40)
    c: Coincident(g41,g8)
    c: Coincident(g41,g20)
    c: Horizontal(g41)
    c: Coincident(g42,g9)
    c: Coincident(g42,g23)
    c: Horizontal(g42)
    c: Coincident(g43,g9)
    c: Coincident(g43,g23)
    c: Horizontal(g43)
    c: Coincident(g44,g10)
    c: Coincident(g44,g22)
    c: Horizontal(g44)
    c: Coincident(g45,g10)
    c: Coincident(g45,g22)
    c: Horizontal(g45)
    c: Coincident(g46,g11)
    c: Coincident(g46,g21)
    c: Horizontal(g46)
    c: Coincident(g47,g11)
    c: Coincident(g47,g21)
    c: Horizontal(g47)
FEATURE [Part::Extrusion] Extrude023
  Base = -> Sketch032
  Dir = (1,-2e-16,2e-16)
  DirMode = 2
  FaceMakerClass = Part::FaceMakerBullseye
  LengthFwd = 19
  LengthRev = 0
  Placement = pos=(-19,0,0) rot=(0,0,1;0rad)
  Solid = true
  Symmetric = false
FEATURE [Part::Fillet] Fillet023
  Base = -> Extrude023
  Edges = 24 edges r=1.49: [Edge6,Edge11,Edge18,Edge23,Edge30,Edge35,Edge42,Edge47,Edge54,Edge59,Edge66,Edge71,Edge78,Edge83,Edge90,Edge95,Edge102,Edge107,Edge114,Edge119,Edge126,Edge131,Edge138,Edge143]
  Placement = pos=(0,0.05,0) rot=(0,0,1;0rad)
FEATURE [Part::Cut] Cut014  label="bottom003"
  Base = -> Cut007
  Tool = -> Fusion047
FEATURE [Part::Cut] Cut021  label="bottom004"
  Base = -> Cut014
  Tool = -> Fillet023
FEATURE [Sketcher::SketchObject] Sketch033
  FullyConstrained = true
  Placement = pos=(117,19,0) rot=(0.57735,0.57735,0.57735;2.0944rad)
  sketch-geometry (8):
    g0: LineSegment StartX=-49.19 StartY=69.25 StartZ=0 EndX=-49.19 EndY=66.25 EndZ=0
    g1: LineSegment StartX=-49.19 StartY=5.75 StartZ=0 EndX=-49.19 EndY=2.75 EndZ=0
    g2: ArcOfCircle CenterX=-1.5 CenterY=67.75 CenterZ=0 NormalX=0 NormalY=0 NormalZ=1 AngleXU=0 Radius=1.5 StartAngle=4.71239 EndAngle=7.85398
    g3: ArcOfCircle CenterX=-1.5 CenterY=4.25 CenterZ=0 NormalX=0 NormalY=0 NormalZ=1 AngleXU=0 Radius=1.5 StartAngle=4.71239 EndAngle=7.85398
    g4: LineSegment StartX=-49.19 StartY=69.25 StartZ=0 EndX=-1.5 EndY=69.25 EndZ=0
    g5: LineSegment StartX=-49.19 StartY=66.25 StartZ=0 EndX=-1.5 EndY=66.25 EndZ=0
    g6: LineSegment StartX=-49.19 StartY=5.75 StartZ=0 EndX=-1.5 EndY=5.75 EndZ=0
    g7: LineSegment StartX=-49.19 StartY=2.75 StartZ=0 EndX=-1.5 EndY=2.75 EndZ=0
  constraints (19):
    c: Vertical(g0)
    c: Distance(g0) = 3
    c: Block(g0)
    c: Vertical(g1)
    c: Block(g2)
    c: Block(g3)
    c: Block(g1)
    c: Coincident(g4,g0)
    c: Coincident(g4,g2)
    c: Horizontal(g4)
    c: Coincident(g5,g0)
    c: Coincident(g5,g2)
    c: Horizontal(g5)
    c: Coincident(g6,g1)
    c: Coincident(g6,g3)
    c: Horizontal(g6)
    c: Coincident(g7,g1)
    c: Coincident(g7,g3)
    c: Horizontal(g7)
FEATURE [Sketcher::SketchObject] Sketch034
  FullyConstrained = true
  Placement = pos=(117,19,0) rot=(0.57735,0.57735,0.57735;2.0944rad)
  sketch-geometry (8):
    g0: LineSegment StartX=-49.19 StartY=63.5 StartZ=0 EndX=-49.19 EndY=60.5 EndZ=0
    g1: LineSegment StartX=-49.19 StartY=11.5 StartZ=0 EndX=-49.19 EndY=8.5 EndZ=0
    g2: ArcOfCircle CenterX=-1.5 CenterY=62 CenterZ=0 NormalX=0 NormalY=0 NormalZ=1 AngleXU=0 Radius=1.5 StartAngle=4.71239 EndAngle=7.85398
    g3: ArcOfCircle CenterX=-1.5 CenterY=10 CenterZ=0 NormalX=0 NormalY=0 NormalZ=1 AngleXU=0 Radius=1.5 StartAngle=4.71239 EndAngle=7.85398
    g4: LineSegment StartX=-49.19 StartY=63.5 StartZ=0 EndX=-1.5 EndY=63.5 EndZ=0
    g5: LineSegment StartX=-49.19 StartY=60.5 StartZ=0 EndX=-1.5 EndY=60.5 EndZ=0
    g6: LineSegment StartX=-49.19 StartY=11.5 StartZ=0 EndX=-1.5 EndY=11.5 EndZ=0
    g7: LineSegment StartX=-49.19 StartY=8.5 StartZ=0 EndX=-1.5 EndY=8.5 EndZ=0
  constraints (19):
    c: Vertical(g0)
    c: Distance(g0) = 3
    c: Vertical(g1)
    c: Block(g1)
    c: Block(g2)
    c: Block(g3)
    c: Block(g0)
    c: Coincident(g4,g0)
    c: Coincident(g4,g2)
    c: Horizontal(g4)
    c: Coincident(g5,g0)
    c: Coincident(g5,g2)
    c: Horizontal(g5)
    c: Coincident(g6,g1)
    c: Coincident(g6,g3)
    c: Horizontal(g6)
    c: Coincident(g7,g1)
    c: Coincident(g7,g3)
    c: Horizontal(g7)
FEATURE [Part::Extrusion] Extrude024
  Base = -> Sketch033
  Dir = (1,0,0)
  DirMode = 2
  FaceMakerClass = Part::FaceMakerBullseye
  LengthFwd = 10
  LengthRev = 0
  Solid = true
  Symmetric = false
FEATURE [Part::Extrusion] Extrude025
  Base = -> Sketch034
  Dir = (1,0,0)
  DirMode = 2
  FaceMakerClass = Part::FaceMakerBullseye
  LengthFwd = 10
  LengthRev = 0
  Solid = true
  Symmetric = false
FEATURE [Part::Fillet] Fillet024  label="removeFromtMoreFrontCaseScrewRetainers"
  Base = -> Extrude024
  Edges = 4 edges r=1.49: [Edge6,Edge11,Edge18,Edge23]
  Placement = pos=(-11,0,0) rot=(0,0,1;0rad)
FEATURE [Part::Fillet] Fillet025  label="removeFromtMoreFrontCaseScrewRetainers001"
  Base = -> Extrude025
  Edges = 4 edges r=1.49: [Edge6,Edge11,Edge18,Edge23]
  Placement = pos=(-19,0,0) rot=(0,0,1;0rad)
FEATURE [Part::Cut] Cut022
  Base = -> Cut015
  Tool = -> Fillet025
FEATURE [Part::Cut] Cut023  label="screwRetainers"
  Base = -> Cut022
  Tool = -> Fillet024
FEATURE [Part::MultiFuse] Fusion056  label="bottom005"
  Shapes = -> [Fusion044,Cut021]
